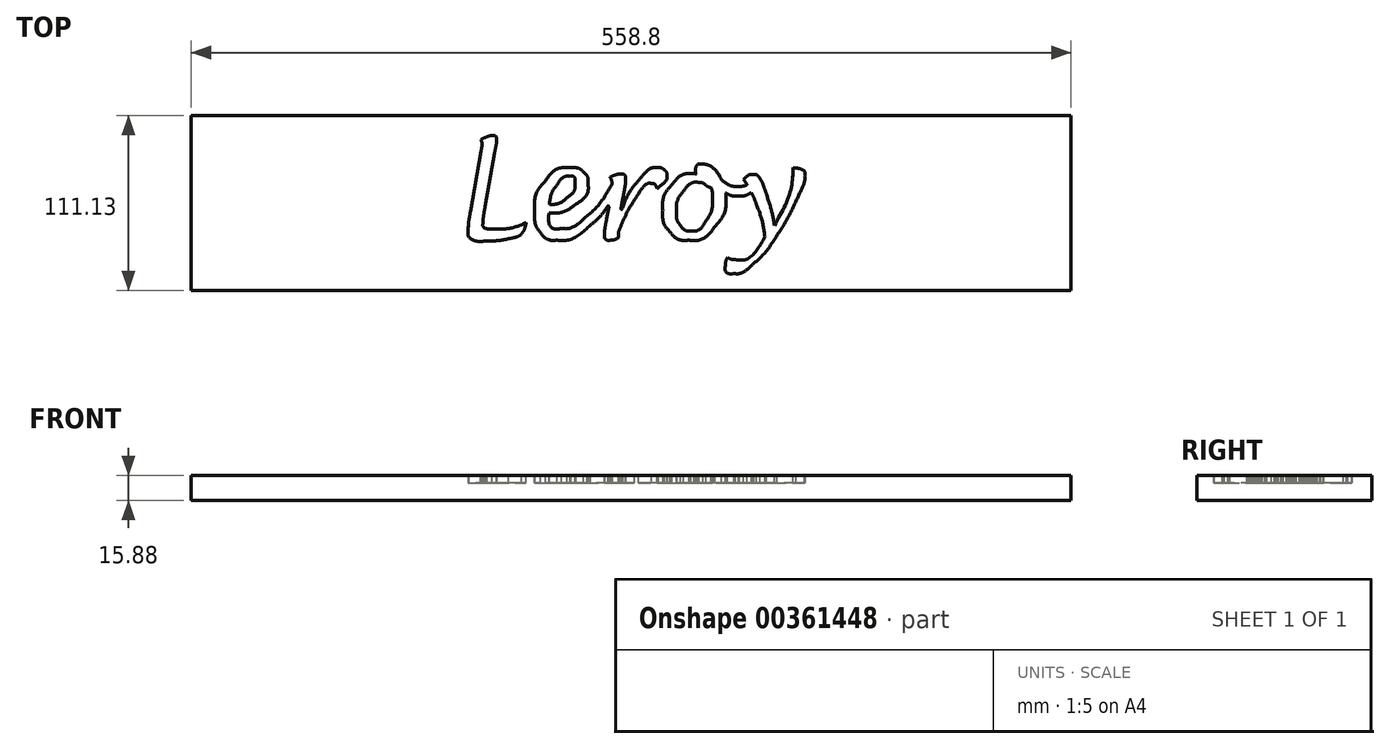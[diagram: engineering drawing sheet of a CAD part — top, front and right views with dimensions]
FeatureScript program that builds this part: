
annotation { "Feature Type Name" : "Feature", "Feature Type Description" : "" }
export const myFeature = defineFeature(function(context is Context, id is Id, definition is map)
    precondition{}
    {
        {
            var Q0;
            Q0=qCreatedBy(makeId("Top.planeOp"),FACE);
            var sketch = newSketch(context, id + "F0", { "sketchPlane" : qUnion([Q0])});
            skLineSegment(sketch, "E0.bottom", {"start": v(12.7, 0) * mm, "end": v(546.1, 0) * mm});
            skLineSegment(sketch, "E0.top", {"start": v(12.7, 609.6) * mm, "end": v(546.1, 609.6) * mm});
            skLineSegment(sketch, "E0.left", {"start": v(0, 12.7) * mm, "end": v(0, 596.9) * mm});
            skLineSegment(sketch, "E0.right", {"start": v(558.8, 12.7) * mm, "end": v(558.8, 596.9) * mm});
            skPoint(sketch, "E1.visualSharp", {"position": v(0, 609.6) * mm});
            skArc(sketch, "E1.filletArc", {"start": v(12.7, 609.6) * mm, "mid": v(3.72, 605.88) * mm, "end": v(0, 596.9) * mm});
            skPoint(sketch, "E2.visualSharp", {"position": v(0, 0) * mm});
            skArc(sketch, "E2.filletArc", {"start": v(0, 12.7) * mm, "mid": v(3.72, 3.72) * mm, "end": v(12.7, 0) * mm});
            skPoint(sketch, "E3.visualSharp", {"position": v(558.8, 0) * mm});
            skArc(sketch, "E3.filletArc", {"start": v(546.1, 0) * mm, "mid": v(555.08, 3.72) * mm, "end": v(558.8, 12.7) * mm});
            skPoint(sketch, "E4.visualSharp", {"position": v(558.8, 609.6) * mm});
            skArc(sketch, "E4.filletArc", {"start": v(558.8, 596.9) * mm, "mid": v(555.08, 605.88) * mm, "end": v(546.1, 609.6) * mm});
            skSolve(sketch);
        }
        {
            var Q0;
            Q0=makeQuery(id+"F0.imprint","IMPRINT",FACE,{"disambiguationData":[TD([[makeQuery(id+"F0.imprint","IMPRINT",EDGE,{"derivedFrom":sQuery(id+"F0.wireOp",EDGE,"E0.bottom")}),1.0]])]});
            extrude(context, id + "F1", {"entities" : qUnion([Q0]), "depth" : 15.88 * mm});
        }
        {
            var Q0;
            Q0=makeQuery(id+"F1.opExtrude","CAP_FACE",FACE,{"disambiguationData":[OSD([sQuery(id+"F0.wireOp",EDGE,"E0.bottom"),sQuery(id+"F0.wireOp",EDGE,"E0.top"),sQuery(id+"F0.wireOp",EDGE,"E0.left"),sQuery(id+"F0.wireOp",EDGE,"E0.right"),sQuery(id+"F0.wireOp",EDGE,"E1.filletArc"),sQuery(id+"F0.wireOp",EDGE,"E2.filletArc"),sQuery(id+"F0.wireOp",EDGE,"E3.filletArc"),sQuery(id+"F0.wireOp",EDGE,"E4.filletArc")])],"isStart":false});
            var sketch = newSketch(context, id + "F2", { "sketchPlane" : qUnion([Q0])});
            skFitSpline(sketch, "E5", {"points": [v(247.46, 485.02) * mm, v(244.22, 485.02) * mm, v(241.38, 482.73) * mm, v(238.94, 478.15) * mm]});
            skFitSpline(sketch, "E6", {"points": [v(238.94, 478.15) * mm, v(236.48, 473.56) * mm, v(235.26, 468.05) * mm, v(235.26, 461.6) * mm]});
            skFitSpline(sketch, "E7", {"points": [v(235.26, 461.6) * mm, v(235.26, 456.87) * mm, v(236.54, 454.5) * mm, v(239.12, 454.5) * mm]});
            skFitSpline(sketch, "E8", {"points": [v(239.12, 454.5) * mm, v(242.2, 454.5) * mm, v(248.34, 462.57) * mm, v(257.6, 478.7) * mm]});
            skFitSpline(sketch, "E9", {"points": [v(257.6, 478.7) * mm, v(257.73, 478.94) * mm, v(258.18, 479.46) * mm, v(258.91, 480.26) * mm]});
            skFitSpline(sketch, "E10", {"points": [v(258.91, 480.26) * mm, v(254.36, 483.44) * mm, v(250.54, 485.02) * mm, v(247.46, 485.02) * mm]});
            skFitSpline(sketch, "E11", {"points": [v(371.38, 485.98) * mm, v(368.47, 485.98) * mm, v(365.74, 484.16) * mm, v(363.18, 480.52) * mm]});
            skFitSpline(sketch, "E12", {"points": [v(363.18, 480.52) * mm, v(360.62, 476.88) * mm, v(359.03, 472.72) * mm, v(358.4, 468.06) * mm]});
            skFitSpline(sketch, "E13", {"points": [v(358.4, 468.06) * mm, v(362.59, 468.32) * mm, v(366.35, 469.82) * mm, v(369.66, 472.53) * mm]});
            skFitSpline(sketch, "E14", {"points": [v(369.66, 472.53) * mm, v(372.98, 475.24) * mm, v(374.64, 478.32) * mm, v(374.64, 481.78) * mm]});
            skFitSpline(sketch, "E15", {"points": [v(374.64, 481.78) * mm, v(374.64, 484.58) * mm, v(373.55, 485.98) * mm, v(371.38, 485.98) * mm]});
            skFitSpline(sketch, "E16", {"points": [v(372.25, 491.45) * mm, v(375.43, 491.45) * mm, v(378, 490.53) * mm, v(379.95, 488.68) * mm]});
            skFitSpline(sketch, "E17", {"points": [v(379.95, 488.68) * mm, v(381.9, 486.84) * mm, v(382.89, 484.38) * mm, v(382.89, 481.3) * mm]});
            skFitSpline(sketch, "E18", {"points": [v(382.89, 481.3) * mm, v(382.89, 476.36) * mm, v(380.3, 472.02) * mm, v(375.12, 468.3) * mm]});
            skFitSpline(sketch, "E19", {"points": [v(375.12, 468.3) * mm, v(369.94, 464.57) * mm, v(364.27, 462.7) * mm, v(358.12, 462.7) * mm]});
            skFitSpline(sketch, "E20", {"points": [v(358.12, 462.7) * mm, v(358.12, 456.15) * mm, v(360.76, 452.87) * mm, v(366.01, 452.87) * mm]});
            skFitSpline(sketch, "E21", {"points": [v(366.01, 452.87) * mm, v(370.84, 452.87) * mm, v(376.2, 455.49) * mm, v(382.13, 460.74) * mm]});
            skFitSpline(sketch, "E22", {"points": [v(382.13, 460.74) * mm, v(388.04, 465.98) * mm, v(393.52, 473.06) * mm, v(398.54, 481.95) * mm]});
            skFitSpline(sketch, "E23", {"points": [v(402.5, 479.62) * mm, v(397.84, 469.55) * mm, v(391.82, 461.33) * mm, v(384.42, 454.98) * mm]});
            skFitSpline(sketch, "E24", {"points": [v(384.42, 454.98) * mm, v(377.03, 448.62) * mm, v(369.98, 445.45) * mm, v(363.3, 445.45) * mm]});
            skFitSpline(sketch, "E25", {"points": [v(363.3, 445.45) * mm, v(358.9, 445.45) * mm, v(355.42, 447.05) * mm, v(352.87, 450.22) * mm]});
            skFitSpline(sketch, "E26", {"points": [v(352.87, 450.22) * mm, v(350.64, 453) * mm, v(349.4, 456.61) * mm, v(349.1, 461.08) * mm]});
            skFitSpline(sketch, "E27", {"points": [v(349.1, 461.08) * mm, v(347.32, 458.56) * mm, v(345.51, 456.33) * mm, v(343.7, 454.35) * mm]});
            skFitSpline(sketch, "E28", {"points": [v(343.7, 454.35) * mm, v(338.24, 448.42) * mm, v(333.27, 445.45) * mm, v(328.8, 445.45) * mm]});
            skFitSpline(sketch, "E29", {"points": [v(328.8, 445.45) * mm, v(325.99, 445.45) * mm, v(323.71, 446.48) * mm, v(322, 448.54) * mm]});
            skFitSpline(sketch, "E30", {"points": [v(322, 448.54) * mm, v(320.27, 450.6) * mm, v(319.41, 453.3) * mm, v(319.41, 456.62) * mm]});
            skFitSpline(sketch, "E31", {"points": [v(319.41, 456.62) * mm, v(319.41, 457.85) * mm, v(319.64, 459.77) * mm, v(320.12, 462.36) * mm]});
            skLineSegment(sketch, "E32", {"start": v(398.54, 481.95) * mm, "end": v(402.5, 479.62) * mm});
            skLineSegment(sketch, "E33", {"start": v(402.5, 479.62) * mm, "end": v(398.54, 481.95) * mm});
            skFitSpline(sketch, "E34", {"points": [v(320.89, 466.68) * mm, v(322, 472.85) * mm, v(322.57, 477.15) * mm, v(322.57, 479.6) * mm]});
            skFitSpline(sketch, "E35", {"points": [v(322.57, 479.6) * mm, v(322.57, 480.87) * mm, v(322.18, 482.24) * mm, v(321.4, 483.7) * mm]});
            skFitSpline(sketch, "E36", {"points": [v(321.4, 483.7) * mm, v(324.84, 484.7) * mm, v(326.97, 485.22) * mm, v(327.78, 485.22) * mm]});
            skFitSpline(sketch, "E37", {"points": [v(327.78, 485.22) * mm, v(329.99, 485.22) * mm, v(331.1, 483.6) * mm, v(331.1, 480.35) * mm]});
            skFitSpline(sketch, "E38", {"points": [v(331.1, 480.35) * mm, v(331.1, 478.32) * mm, v(330.76, 475.38) * mm, v(330.07, 471.54) * mm]});
            skLineSegment(sketch, "E39", {"start": v(320.12, 462.36) * mm, "end": v(320.89, 466.68) * mm});
            skLineSegment(sketch, "E40", {"start": v(320.89, 466.68) * mm, "end": v(320.12, 462.36) * mm});
            skFitSpline(sketch, "E41", {"points": [v(328.7, 463.92) * mm, v(328.05, 460.32) * mm, v(327.73, 458) * mm, v(327.73, 456.92) * mm]});
            skFitSpline(sketch, "E42", {"points": [v(327.73, 456.92) * mm, v(327.73, 454.22) * mm, v(328.7, 452.87) * mm, v(330.64, 452.87) * mm]});
            skFitSpline(sketch, "E43", {"points": [v(330.64, 452.87) * mm, v(333.34, 452.87) * mm, v(337.06, 455.56) * mm, v(341.8, 460.93) * mm]});
            skFitSpline(sketch, "E44", {"points": [v(341.8, 460.93) * mm, v(344.6, 464.12) * mm, v(347.4, 467.87) * mm, v(350.2, 472.2) * mm]});
            skFitSpline(sketch, "E45", {"points": [v(350.2, 472.2) * mm, v(351.28, 476.24) * mm, v(353.16, 479.88) * mm, v(355.83, 483.14) * mm]});
            skFitSpline(sketch, "E46", {"points": [v(355.83, 483.14) * mm, v(360.35, 488.68) * mm, v(365.83, 491.45) * mm, v(372.25, 491.45) * mm]});
            skLineSegment(sketch, "E47", {"start": v(330.07, 471.54) * mm, "end": v(328.7, 463.92) * mm});
            skLineSegment(sketch, "E48", {"start": v(328.7, 463.92) * mm, "end": v(330.07, 471.54) * mm});
            skFitSpline(sketch, "E49", {"points": [v(305.1, 507.84) * mm, v(305.33, 507.84) * mm, v(306.14, 507.78) * mm, v(307.5, 507.65) * mm]});
            skFitSpline(sketch, "E50", {"points": [v(307.5, 507.65) * mm, v(305.64, 504.33) * mm, v(303.76, 499.96) * mm, v(301.86, 494.56) * mm]});
            skFitSpline(sketch, "E51", {"points": [v(319.5, 494.56) * mm, v(322.22, 494.56) * mm, v(324.64, 494.92) * mm, v(326.74, 495.67) * mm]});
            skFitSpline(sketch, "E52", {"points": [v(326.74, 495.67) * mm, v(326.87, 497.05) * mm, v(327.2, 498.41) * mm, v(327.69, 499.77) * mm]});
            skLineSegment(sketch, "E53", {"start": v(301.86, 494.56) * mm, "end": v(319.5, 494.56) * mm});
            skLineSegment(sketch, "E54", {"start": v(319.5, 494.56) * mm, "end": v(301.86, 494.56) * mm});
            skFitSpline(sketch, "E55", {"points": [v(328.67, 499.72) * mm, v(330.08, 499.79) * mm, v(332.2, 500.64) * mm, v(335.04, 502.28) * mm]});
            skFitSpline(sketch, "E56", {"points": [v(335.04, 502.28) * mm, v(337.9, 503.93) * mm, v(340.52, 505.68) * mm, v(342.94, 507.52) * mm]});
            skFitSpline(sketch, "E57", {"points": [v(342.94, 507.52) * mm, v(341.85, 503.08) * mm, v(340.03, 500.06) * mm, v(337.5, 498.48) * mm]});
            skFitSpline(sketch, "E58", {"points": [v(337.5, 498.48) * mm, v(333.26, 493.7) * mm, v(330.34, 491.32) * mm, v(328.76, 491.32) * mm]});
            skFitSpline(sketch, "E59", {"points": [v(328.76, 491.32) * mm, v(327.76, 491.32) * mm, v(327.1, 491.79) * mm, v(326.85, 492.72) * mm]});
            skFitSpline(sketch, "E60", {"points": [v(326.85, 492.72) * mm, v(326.33, 491.05) * mm, v(325.73, 489.92) * mm, v(325.02, 489.33) * mm]});
            skFitSpline(sketch, "E61", {"points": [v(325.02, 489.33) * mm, v(323.92, 488.4) * mm, v(321.98, 487.93) * mm, v(319.18, 487.93) * mm]});
            skLineSegment(sketch, "E62", {"start": v(327.69, 499.77) * mm, "end": v(328.67, 499.72) * mm});
            skLineSegment(sketch, "E63", {"start": v(328.67, 499.72) * mm, "end": v(327.69, 499.77) * mm});
            skFitSpline(sketch, "E64", {"points": [v(300.17, 487.93) * mm, v(300.04, 487.44) * mm, v(299.9, 486.92) * mm, v(299.75, 486.38) * mm]});
            skFitSpline(sketch, "E65", {"points": [v(299.75, 486.38) * mm, v(296.99, 475.84) * mm, v(295.6, 467.88) * mm, v(295.6, 462.47) * mm]});
            skFitSpline(sketch, "E66", {"points": [v(295.6, 462.47) * mm, v(295.6, 456.94) * mm, v(297.3, 454.18) * mm, v(300.68, 454.18) * mm]});
            skFitSpline(sketch, "E67", {"points": [v(300.68, 454.18) * mm, v(302.53, 454.18) * mm, v(304.57, 455.1) * mm, v(306.8, 456.9) * mm]});
            skFitSpline(sketch, "E68", {"points": [v(306.8, 456.9) * mm, v(309.05, 458.71) * mm, v(310.85, 460.91) * mm, v(312.2, 463.5) * mm]});
            skFitSpline(sketch, "E69", {"points": [v(312.2, 463.5) * mm, v(313.35, 461.8) * mm, v(313.92, 460.42) * mm, v(313.92, 459.33) * mm]});
            skFitSpline(sketch, "E70", {"points": [v(313.92, 459.33) * mm, v(313.92, 456.5) * mm, v(311.92, 453.5) * mm, v(307.92, 450.28) * mm]});
            skFitSpline(sketch, "E71", {"points": [v(307.92, 450.28) * mm, v(303.9, 447.06) * mm, v(300.24, 445.45) * mm, v(296.9, 445.45) * mm]});
            skFitSpline(sketch, "E72", {"points": [v(296.9, 445.45) * mm, v(293.88, 445.45) * mm, v(291.42, 446.93) * mm, v(289.56, 449.9) * mm]});
            skFitSpline(sketch, "E73", {"points": [v(289.56, 449.9) * mm, v(287.7, 452.87) * mm, v(286.76, 456.65) * mm, v(286.76, 461.23) * mm]});
            skFitSpline(sketch, "E74", {"points": [v(286.76, 461.23) * mm, v(286.76, 462.58) * mm, v(286.84, 464.08) * mm, v(287.02, 465.75) * mm]});
            skFitSpline(sketch, "E75", {"points": [v(287.02, 465.75) * mm, v(284.81, 462.56) * mm, v(282.47, 459.69) * mm, v(280.01, 457.13) * mm]});
            skFitSpline(sketch, "E76", {"points": [v(280.01, 457.13) * mm, v(274.37, 451.28) * mm, v(269.48, 448.36) * mm, v(265.31, 448.36) * mm]});
            skFitSpline(sketch, "E77", {"points": [v(265.31, 448.36) * mm, v(259.81, 448.36) * mm, v(257.07, 453.3) * mm, v(257.07, 463.23) * mm]});
            skFitSpline(sketch, "E78", {"points": [v(257.07, 463.23) * mm, v(257.07, 465.2) * mm, v(257.14, 467.57) * mm, v(257.28, 470.32) * mm]});
            skFitSpline(sketch, "E79", {"points": [v(257.28, 470.32) * mm, v(255.19, 463.64) * mm, v(251.91, 457.83) * mm, v(247.46, 452.87) * mm]});
            skFitSpline(sketch, "E80", {"points": [v(247.46, 452.87) * mm, v(242.99, 447.92) * mm, v(239.04, 445.45) * mm, v(235.6, 445.45) * mm]});
            skFitSpline(sketch, "E81", {"points": [v(235.6, 445.45) * mm, v(232.88, 445.45) * mm, v(230.72, 446.77) * mm, v(229.15, 449.4) * mm]});
            skFitSpline(sketch, "E82", {"points": [v(229.15, 449.4) * mm, v(227.56, 452.05) * mm, v(226.77, 455.51) * mm, v(226.77, 459.78) * mm]});
            skFitSpline(sketch, "E83", {"points": [v(226.77, 459.78) * mm, v(226.77, 468.13) * mm, v(229.03, 475.5) * mm, v(233.56, 481.87) * mm]});
            skFitSpline(sketch, "E84", {"points": [v(233.56, 481.87) * mm, v(238.09, 488.26) * mm, v(243.35, 491.45) * mm, v(249.38, 491.45) * mm]});
            skFitSpline(sketch, "E85", {"points": [v(249.38, 491.45) * mm, v(253.01, 491.45) * mm, v(256.66, 490.21) * mm, v(260.33, 487.76) * mm]});
            skFitSpline(sketch, "E86", {"points": [v(260.33, 487.76) * mm, v(260.86, 490.19) * mm, v(263.48, 491.4) * mm, v(268.16, 491.4) * mm]});
            skFitSpline(sketch, "E87", {"points": [v(268.16, 491.4) * mm, v(268.26, 491.4) * mm, v(268.96, 491.37) * mm, v(270.27, 491.3) * mm]});
            skFitSpline(sketch, "E88", {"points": [v(270.27, 491.3) * mm, v(268.9, 488.33) * mm, v(267.89, 484.93) * mm, v(267.2, 481.1) * mm]});
            skLineSegment(sketch, "E89", {"start": v(319.18, 487.93) * mm, "end": v(300.17, 487.93) * mm});
            skLineSegment(sketch, "E90", {"start": v(300.17, 487.93) * mm, "end": v(319.18, 487.93) * mm});
            skFitSpline(sketch, "E91", {"points": [v(266.62, 477.77) * mm, v(265.96, 474.15) * mm, v(265.63, 469.88) * mm, v(265.63, 464.94) * mm]});
            skFitSpline(sketch, "E92", {"points": [v(265.63, 464.94) * mm, v(265.63, 459.77) * mm, v(266.57, 457.18) * mm, v(268.44, 457.18) * mm]});
            skFitSpline(sketch, "E93", {"points": [v(268.44, 457.18) * mm, v(270.76, 457.18) * mm, v(274.05, 459.48) * mm, v(278.32, 464.1) * mm]});
            skFitSpline(sketch, "E94", {"points": [v(278.32, 464.1) * mm, v(281.96, 468.04) * mm, v(285.66, 473) * mm, v(289.42, 478.98) * mm]});
            skFitSpline(sketch, "E95", {"points": [v(289.42, 478.98) * mm, v(289.7, 480.18) * mm, v(290, 481.4) * mm, v(290.32, 482.69) * mm]});
            skLineSegment(sketch, "E96", {"start": v(267.2, 481.1) * mm, "end": v(266.62, 477.77) * mm});
            skLineSegment(sketch, "E97", {"start": v(266.62, 477.77) * mm, "end": v(267.2, 481.1) * mm});
            skFitSpline(sketch, "E98", {"points": [v(286.65, 487.93) * mm, v(284.3, 487.93) * mm, v(282.1, 487.54) * mm, v(280.04, 486.76) * mm]});
            skFitSpline(sketch, "E99", {"points": [v(280.04, 486.76) * mm, v(281.5, 490.38) * mm, v(282.72, 492.6) * mm, v(283.72, 493.38) * mm]});
            skFitSpline(sketch, "E100", {"points": [v(283.72, 493.38) * mm, v(284.71, 494.16) * mm, v(286.34, 494.56) * mm, v(288.6, 494.56) * mm]});
            skLineSegment(sketch, "E101", {"start": v(290.32, 482.69) * mm, "end": v(291.82, 487.93) * mm});
            skLineSegment(sketch, "E102", {"start": v(291.82, 487.93) * mm, "end": v(286.65, 487.93) * mm});
            skFitSpline(sketch, "E103", {"points": [v(293.99, 497.12) * mm, v(295.02, 501) * mm, v(296.33, 503.76) * mm, v(297.95, 505.4) * mm]});
            skFitSpline(sketch, "E104", {"points": [v(297.95, 505.4) * mm, v(299.55, 507.03) * mm, v(301.94, 507.84) * mm, v(305.1, 507.84) * mm]});
            skLineSegment(sketch, "E105", {"start": v(288.6, 494.56) * mm, "end": v(293.33, 494.56) * mm});
            skLineSegment(sketch, "E106", {"start": v(293.33, 494.56) * mm, "end": v(293.99, 497.12) * mm});
            skFitSpline(sketch, "E107", {"points": [v(178.41, 506.2) * mm, v(181.96, 506.2) * mm, v(186.85, 506.6) * mm, v(193.08, 507.4) * mm]});
            skFitSpline(sketch, "E108", {"points": [v(188.04, 478.85) * mm, v(200.42, 488.81) * mm, v(207.85, 498.44) * mm, v(210.33, 507.7) * mm]});
            skFitSpline(sketch, "E109", {"points": [v(210.33, 507.7) * mm, v(214.42, 505.56) * mm, v(216.46, 503.26) * mm, v(216.46, 500.79) * mm]});
            skFitSpline(sketch, "E110", {"points": [v(216.46, 500.79) * mm, v(216.46, 499.37) * mm, v(213.98, 496.13) * mm, v(209, 491.1) * mm]});
            skFitSpline(sketch, "E111", {"points": [v(209, 491.1) * mm, v(204.02, 486.08) * mm, v(199.1, 481.73) * mm, v(194.23, 478.07) * mm]});
            skFitSpline(sketch, "E112", {"points": [v(194.23, 478.07) * mm, v(198.39, 469.54) * mm, v(202.46, 462.52) * mm, v(206.43, 457.03) * mm]});
            skFitSpline(sketch, "E113", {"points": [v(206.43, 457.03) * mm, v(210.4, 451.54) * mm, v(213.38, 448.8) * mm, v(215.37, 448.8) * mm]});
            skFitSpline(sketch, "E114", {"points": [v(215.37, 448.8) * mm, v(217.55, 448.8) * mm, v(220.39, 450.27) * mm, v(223.87, 453.22) * mm]});
            skLineSegment(sketch, "E115", {"start": v(193.08, 507.4) * mm, "end": v(188.04, 478.85) * mm});
            skLineSegment(sketch, "E116", {"start": v(188.04, 478.85) * mm, "end": v(193.08, 507.4) * mm});
            skFitSpline(sketch, "E117", {"points": [v(223.98, 451.1) * mm, v(223.98, 449.09) * mm, v(222.68, 446.98) * mm, v(220.08, 444.73) * mm]});
            skFitSpline(sketch, "E118", {"points": [v(220.08, 444.73) * mm, v(217.49, 442.5) * mm, v(214.96, 441.38) * mm, v(212.51, 441.38) * mm]});
            skFitSpline(sketch, "E119", {"points": [v(212.51, 441.38) * mm, v(206.3, 441.38) * mm, v(197.85, 452.5) * mm, v(187.18, 474.76) * mm]});
            skLineSegment(sketch, "E120", {"start": v(223.87, 453.22) * mm, "end": v(223.98, 451.1) * mm});
            skLineSegment(sketch, "E121", {"start": v(223.98, 451.1) * mm, "end": v(223.87, 453.22) * mm});
            skFitSpline(sketch, "E122", {"points": [v(183.9, 454.8) * mm, v(183.48, 452.44) * mm, v(183.27, 450.88) * mm, v(183.27, 450.14) * mm]});
            skFitSpline(sketch, "E123", {"points": [v(183.27, 450.14) * mm, v(183.27, 449.5) * mm, v(183.42, 448.6) * mm, v(183.73, 447.42) * mm]});
            skFitSpline(sketch, "E124", {"points": [v(183.73, 447.42) * mm, v(180.96, 445.82) * mm, v(178.55, 445.01) * mm, v(176.52, 445.01) * mm]});
            skFitSpline(sketch, "E125", {"points": [v(176.52, 445.01) * mm, v(174.84, 445.01) * mm, v(174, 445.83) * mm, v(174, 447.45) * mm]});
            skFitSpline(sketch, "E126", {"points": [v(174, 447.45) * mm, v(174, 448.08) * mm, v(174.25, 449.8) * mm, v(174.74, 452.56) * mm]});
            skLineSegment(sketch, "E127", {"start": v(187.18, 474.76) * mm, "end": v(183.9, 454.8) * mm});
            skLineSegment(sketch, "E128", {"start": v(183.9, 454.8) * mm, "end": v(187.18, 474.76) * mm});
            skFitSpline(sketch, "E129", {"points": [v(183.17, 499.25) * mm, v(181.66, 498.94) * mm, v(180, 498.79) * mm, v(178.17, 498.79) * mm]});
            skFitSpline(sketch, "E130", {"points": [v(178.17, 498.79) * mm, v(174.1, 498.79) * mm, v(171.7, 502.02) * mm, v(170.94, 508.51) * mm]});
            skLineSegment(sketch, "E131", {"start": v(174.74, 452.56) * mm, "end": v(183.17, 499.25) * mm});
            skLineSegment(sketch, "E132", {"start": v(183.17, 499.25) * mm, "end": v(174.74, 452.56) * mm});
            skFitSpline(sketch, "E133", {"points": [v(247.46, 485.02) * mm, v(244.22, 485.02) * mm, v(241.38, 482.73) * mm, v(238.94, 478.15) * mm]});
            skFitSpline(sketch, "E134", {"points": [v(238.94, 478.15) * mm, v(236.48, 473.56) * mm, v(235.26, 468.05) * mm, v(235.26, 461.6) * mm]});
            skFitSpline(sketch, "E135", {"points": [v(235.26, 461.6) * mm, v(235.26, 456.87) * mm, v(236.54, 454.5) * mm, v(239.12, 454.5) * mm]});
            skFitSpline(sketch, "E136", {"points": [v(239.12, 454.5) * mm, v(242.2, 454.5) * mm, v(248.34, 462.57) * mm, v(257.6, 478.7) * mm]});
            skFitSpline(sketch, "E137", {"points": [v(257.6, 478.7) * mm, v(257.73, 478.94) * mm, v(258.18, 479.46) * mm, v(258.91, 480.26) * mm]});
            skFitSpline(sketch, "E138", {"points": [v(258.91, 480.26) * mm, v(254.36, 483.44) * mm, v(250.54, 485.02) * mm, v(247.46, 485.02) * mm]});
            skFitSpline(sketch, "E139", {"points": [v(371.38, 485.98) * mm, v(368.47, 485.98) * mm, v(365.74, 484.16) * mm, v(363.18, 480.52) * mm]});
            skFitSpline(sketch, "E140", {"points": [v(363.18, 480.52) * mm, v(360.62, 476.88) * mm, v(359.03, 472.72) * mm, v(358.4, 468.06) * mm]});
            skFitSpline(sketch, "E141", {"points": [v(358.4, 468.06) * mm, v(362.59, 468.32) * mm, v(366.35, 469.82) * mm, v(369.66, 472.53) * mm]});
            skFitSpline(sketch, "E142", {"points": [v(369.66, 472.53) * mm, v(372.98, 475.24) * mm, v(374.64, 478.32) * mm, v(374.64, 481.78) * mm]});
            skFitSpline(sketch, "E143", {"points": [v(374.64, 481.78) * mm, v(374.64, 484.58) * mm, v(373.55, 485.98) * mm, v(371.38, 485.98) * mm]});
            skFitSpline(sketch, "E144", {"points": [v(372.25, 491.45) * mm, v(375.43, 491.45) * mm, v(378, 490.53) * mm, v(379.95, 488.68) * mm]});
            skFitSpline(sketch, "E145", {"points": [v(379.95, 488.68) * mm, v(381.9, 486.84) * mm, v(382.89, 484.38) * mm, v(382.89, 481.3) * mm]});
            skFitSpline(sketch, "E146", {"points": [v(382.89, 481.3) * mm, v(382.89, 476.36) * mm, v(380.3, 472.02) * mm, v(375.12, 468.3) * mm]});
            skFitSpline(sketch, "E147", {"points": [v(375.12, 468.3) * mm, v(369.94, 464.57) * mm, v(364.27, 462.7) * mm, v(358.12, 462.7) * mm]});
            skFitSpline(sketch, "E148", {"points": [v(358.12, 462.7) * mm, v(358.12, 456.15) * mm, v(360.76, 452.87) * mm, v(366.01, 452.87) * mm]});
            skFitSpline(sketch, "E149", {"points": [v(366.01, 452.87) * mm, v(370.84, 452.87) * mm, v(376.2, 455.49) * mm, v(382.13, 460.74) * mm]});
            skFitSpline(sketch, "E150", {"points": [v(382.13, 460.74) * mm, v(388.04, 465.98) * mm, v(393.52, 473.06) * mm, v(398.54, 481.95) * mm]});
            skFitSpline(sketch, "E151", {"points": [v(402.5, 479.62) * mm, v(397.84, 469.55) * mm, v(391.82, 461.33) * mm, v(384.42, 454.98) * mm]});
            skFitSpline(sketch, "E152", {"points": [v(384.42, 454.98) * mm, v(377.03, 448.62) * mm, v(369.98, 445.45) * mm, v(363.3, 445.45) * mm]});
            skFitSpline(sketch, "E153", {"points": [v(363.3, 445.45) * mm, v(358.9, 445.45) * mm, v(355.42, 447.05) * mm, v(352.87, 450.22) * mm]});
            skFitSpline(sketch, "E154", {"points": [v(352.87, 450.22) * mm, v(350.64, 453) * mm, v(349.4, 456.61) * mm, v(349.1, 461.08) * mm]});
            skFitSpline(sketch, "E155", {"points": [v(349.1, 461.08) * mm, v(347.32, 458.56) * mm, v(345.51, 456.33) * mm, v(343.7, 454.35) * mm]});
            skFitSpline(sketch, "E156", {"points": [v(343.7, 454.35) * mm, v(338.24, 448.42) * mm, v(333.27, 445.45) * mm, v(328.8, 445.45) * mm]});
            skFitSpline(sketch, "E157", {"points": [v(328.8, 445.45) * mm, v(325.99, 445.45) * mm, v(323.71, 446.48) * mm, v(322, 448.54) * mm]});
            skFitSpline(sketch, "E158", {"points": [v(322, 448.54) * mm, v(320.27, 450.6) * mm, v(319.41, 453.3) * mm, v(319.41, 456.62) * mm]});
            skFitSpline(sketch, "E159", {"points": [v(319.41, 456.62) * mm, v(319.41, 457.85) * mm, v(319.64, 459.77) * mm, v(320.12, 462.36) * mm]});
            skFitSpline(sketch, "E160", {"points": [v(320.89, 466.68) * mm, v(322, 472.85) * mm, v(322.57, 477.15) * mm, v(322.57, 479.6) * mm]});
            skFitSpline(sketch, "E161", {"points": [v(322.57, 479.6) * mm, v(322.57, 480.87) * mm, v(322.18, 482.24) * mm, v(321.4, 483.7) * mm]});
            skFitSpline(sketch, "E162", {"points": [v(321.4, 483.7) * mm, v(324.84, 484.7) * mm, v(326.97, 485.22) * mm, v(327.78, 485.22) * mm]});
            skFitSpline(sketch, "E163", {"points": [v(327.78, 485.22) * mm, v(329.99, 485.22) * mm, v(331.1, 483.6) * mm, v(331.1, 480.35) * mm]});
            skFitSpline(sketch, "E164", {"points": [v(331.1, 480.35) * mm, v(331.1, 478.32) * mm, v(330.76, 475.38) * mm, v(330.07, 471.54) * mm]});
            skFitSpline(sketch, "E165", {"points": [v(328.7, 463.92) * mm, v(328.05, 460.32) * mm, v(327.73, 458) * mm, v(327.73, 456.92) * mm]});
            skFitSpline(sketch, "E166", {"points": [v(327.73, 456.92) * mm, v(327.73, 454.22) * mm, v(328.7, 452.87) * mm, v(330.64, 452.87) * mm]});
            skFitSpline(sketch, "E167", {"points": [v(330.64, 452.87) * mm, v(333.34, 452.87) * mm, v(337.06, 455.56) * mm, v(341.8, 460.93) * mm]});
            skFitSpline(sketch, "E168", {"points": [v(341.8, 460.93) * mm, v(344.6, 464.12) * mm, v(347.4, 467.87) * mm, v(350.2, 472.2) * mm]});
            skFitSpline(sketch, "E169", {"points": [v(350.2, 472.2) * mm, v(351.28, 476.24) * mm, v(353.16, 479.88) * mm, v(355.83, 483.14) * mm]});
            skFitSpline(sketch, "E170", {"points": [v(355.83, 483.14) * mm, v(360.35, 488.68) * mm, v(365.83, 491.45) * mm, v(372.25, 491.45) * mm]});
            skFitSpline(sketch, "E171", {"points": [v(305.1, 507.84) * mm, v(305.33, 507.84) * mm, v(306.14, 507.78) * mm, v(307.5, 507.65) * mm]});
            skFitSpline(sketch, "E172", {"points": [v(307.5, 507.65) * mm, v(305.64, 504.33) * mm, v(303.76, 499.96) * mm, v(301.86, 494.56) * mm]});
            skFitSpline(sketch, "E173", {"points": [v(319.5, 494.56) * mm, v(322.22, 494.56) * mm, v(324.64, 494.92) * mm, v(326.74, 495.67) * mm]});
            skFitSpline(sketch, "E174", {"points": [v(326.74, 495.67) * mm, v(326.87, 497.05) * mm, v(327.2, 498.41) * mm, v(327.69, 499.77) * mm]});
            skFitSpline(sketch, "E175", {"points": [v(328.67, 499.72) * mm, v(330.08, 499.79) * mm, v(332.2, 500.64) * mm, v(335.04, 502.28) * mm]});
            skFitSpline(sketch, "E176", {"points": [v(335.04, 502.28) * mm, v(337.9, 503.93) * mm, v(340.52, 505.68) * mm, v(342.94, 507.52) * mm]});
            skFitSpline(sketch, "E177", {"points": [v(342.94, 507.52) * mm, v(341.85, 503.08) * mm, v(340.03, 500.06) * mm, v(337.5, 498.48) * mm]});
            skFitSpline(sketch, "E178", {"points": [v(337.5, 498.48) * mm, v(333.26, 493.7) * mm, v(330.34, 491.32) * mm, v(328.76, 491.32) * mm]});
            skFitSpline(sketch, "E179", {"points": [v(328.76, 491.32) * mm, v(327.76, 491.32) * mm, v(327.1, 491.79) * mm, v(326.85, 492.72) * mm]});
            skFitSpline(sketch, "E180", {"points": [v(326.85, 492.72) * mm, v(326.33, 491.05) * mm, v(325.73, 489.92) * mm, v(325.02, 489.33) * mm]});
            skFitSpline(sketch, "E181", {"points": [v(325.02, 489.33) * mm, v(323.92, 488.4) * mm, v(321.98, 487.93) * mm, v(319.18, 487.93) * mm]});
            skFitSpline(sketch, "E182", {"points": [v(300.17, 487.93) * mm, v(300.04, 487.44) * mm, v(299.9, 486.92) * mm, v(299.75, 486.38) * mm]});
            skFitSpline(sketch, "E183", {"points": [v(299.75, 486.38) * mm, v(296.99, 475.84) * mm, v(295.6, 467.88) * mm, v(295.6, 462.47) * mm]});
            skFitSpline(sketch, "E184", {"points": [v(295.6, 462.47) * mm, v(295.6, 456.94) * mm, v(297.3, 454.18) * mm, v(300.68, 454.18) * mm]});
            skFitSpline(sketch, "E185", {"points": [v(300.68, 454.18) * mm, v(302.53, 454.18) * mm, v(304.57, 455.1) * mm, v(306.8, 456.9) * mm]});
            skFitSpline(sketch, "E186", {"points": [v(306.8, 456.9) * mm, v(309.05, 458.71) * mm, v(310.85, 460.91) * mm, v(312.2, 463.5) * mm]});
            skFitSpline(sketch, "E187", {"points": [v(312.2, 463.5) * mm, v(313.35, 461.8) * mm, v(313.92, 460.42) * mm, v(313.92, 459.33) * mm]});
            skFitSpline(sketch, "E188", {"points": [v(313.92, 459.33) * mm, v(313.92, 456.5) * mm, v(311.92, 453.5) * mm, v(307.92, 450.28) * mm]});
            skFitSpline(sketch, "E189", {"points": [v(307.92, 450.28) * mm, v(303.9, 447.06) * mm, v(300.24, 445.45) * mm, v(296.9, 445.45) * mm]});
            skFitSpline(sketch, "E190", {"points": [v(296.9, 445.45) * mm, v(293.88, 445.45) * mm, v(291.42, 446.93) * mm, v(289.56, 449.9) * mm]});
            skFitSpline(sketch, "E191", {"points": [v(289.56, 449.9) * mm, v(287.7, 452.87) * mm, v(286.76, 456.65) * mm, v(286.76, 461.23) * mm]});
            skFitSpline(sketch, "E192", {"points": [v(286.76, 461.23) * mm, v(286.76, 462.58) * mm, v(286.84, 464.08) * mm, v(287.02, 465.75) * mm]});
            skFitSpline(sketch, "E193", {"points": [v(287.02, 465.75) * mm, v(284.81, 462.56) * mm, v(282.47, 459.69) * mm, v(280.01, 457.13) * mm]});
            skFitSpline(sketch, "E194", {"points": [v(280.01, 457.13) * mm, v(274.37, 451.28) * mm, v(269.48, 448.36) * mm, v(265.31, 448.36) * mm]});
            skFitSpline(sketch, "E195", {"points": [v(265.31, 448.36) * mm, v(259.81, 448.36) * mm, v(257.07, 453.3) * mm, v(257.07, 463.23) * mm]});
            skFitSpline(sketch, "E196", {"points": [v(257.07, 463.23) * mm, v(257.07, 465.2) * mm, v(257.14, 467.57) * mm, v(257.28, 470.32) * mm]});
            skFitSpline(sketch, "E197", {"points": [v(257.28, 470.32) * mm, v(255.19, 463.64) * mm, v(251.91, 457.83) * mm, v(247.46, 452.87) * mm]});
            skFitSpline(sketch, "E198", {"points": [v(247.46, 452.87) * mm, v(242.99, 447.92) * mm, v(239.04, 445.45) * mm, v(235.6, 445.45) * mm]});
            skFitSpline(sketch, "E199", {"points": [v(235.6, 445.45) * mm, v(232.88, 445.45) * mm, v(230.72, 446.77) * mm, v(229.15, 449.4) * mm]});
            skFitSpline(sketch, "E200", {"points": [v(229.15, 449.4) * mm, v(227.56, 452.05) * mm, v(226.77, 455.51) * mm, v(226.77, 459.78) * mm]});
            skFitSpline(sketch, "E201", {"points": [v(226.77, 459.78) * mm, v(226.77, 468.13) * mm, v(229.03, 475.5) * mm, v(233.56, 481.87) * mm]});
            skFitSpline(sketch, "E202", {"points": [v(233.56, 481.87) * mm, v(238.09, 488.26) * mm, v(243.35, 491.45) * mm, v(249.38, 491.45) * mm]});
            skFitSpline(sketch, "E203", {"points": [v(249.38, 491.45) * mm, v(253.01, 491.45) * mm, v(256.66, 490.21) * mm, v(260.33, 487.76) * mm]});
            skFitSpline(sketch, "E204", {"points": [v(260.33, 487.76) * mm, v(260.86, 490.19) * mm, v(263.48, 491.4) * mm, v(268.16, 491.4) * mm]});
            skFitSpline(sketch, "E205", {"points": [v(268.16, 491.4) * mm, v(268.26, 491.4) * mm, v(268.96, 491.37) * mm, v(270.27, 491.3) * mm]});
            skFitSpline(sketch, "E206", {"points": [v(270.27, 491.3) * mm, v(268.9, 488.33) * mm, v(267.89, 484.93) * mm, v(267.2, 481.1) * mm]});
            skFitSpline(sketch, "E207", {"points": [v(266.62, 477.77) * mm, v(265.96, 474.15) * mm, v(265.63, 469.88) * mm, v(265.63, 464.94) * mm]});
            skFitSpline(sketch, "E208", {"points": [v(265.63, 464.94) * mm, v(265.63, 459.77) * mm, v(266.57, 457.18) * mm, v(268.44, 457.18) * mm]});
            skFitSpline(sketch, "E209", {"points": [v(268.44, 457.18) * mm, v(270.76, 457.18) * mm, v(274.05, 459.48) * mm, v(278.32, 464.1) * mm]});
            skFitSpline(sketch, "E210", {"points": [v(278.32, 464.1) * mm, v(281.96, 468.04) * mm, v(285.66, 473) * mm, v(289.42, 478.98) * mm]});
            skFitSpline(sketch, "E211", {"points": [v(289.42, 478.98) * mm, v(289.7, 480.18) * mm, v(290, 481.4) * mm, v(290.32, 482.69) * mm]});
            skFitSpline(sketch, "E212", {"points": [v(286.65, 487.93) * mm, v(284.3, 487.93) * mm, v(282.1, 487.54) * mm, v(280.04, 486.76) * mm]});
            skFitSpline(sketch, "E213", {"points": [v(280.04, 486.76) * mm, v(281.5, 490.38) * mm, v(282.72, 492.6) * mm, v(283.72, 493.38) * mm]});
            skFitSpline(sketch, "E214", {"points": [v(283.72, 493.38) * mm, v(284.71, 494.16) * mm, v(286.34, 494.56) * mm, v(288.6, 494.56) * mm]});
            skFitSpline(sketch, "E215", {"points": [v(293.99, 497.12) * mm, v(295.02, 501) * mm, v(296.33, 503.76) * mm, v(297.95, 505.4) * mm]});
            skFitSpline(sketch, "E216", {"points": [v(297.95, 505.4) * mm, v(299.55, 507.03) * mm, v(301.94, 507.84) * mm, v(305.1, 507.84) * mm]});
            skFitSpline(sketch, "E217", {"points": [v(170.94, 508.51) * mm, v(173.27, 506.97) * mm, v(175.75, 506.2) * mm, v(178.41, 506.2) * mm]});
            skFitSpline(sketch, "E218", {"points": [v(178.41, 506.2) * mm, v(181.96, 506.2) * mm, v(186.85, 506.6) * mm, v(193.08, 507.4) * mm]});
            skFitSpline(sketch, "E219", {"points": [v(188.04, 478.85) * mm, v(200.42, 488.81) * mm, v(207.85, 498.44) * mm, v(210.33, 507.7) * mm]});
            skFitSpline(sketch, "E220", {"points": [v(210.33, 507.7) * mm, v(214.42, 505.56) * mm, v(216.46, 503.26) * mm, v(216.46, 500.79) * mm]});
            skFitSpline(sketch, "E221", {"points": [v(216.46, 500.79) * mm, v(216.46, 499.37) * mm, v(213.98, 496.13) * mm, v(209, 491.1) * mm]});
            skFitSpline(sketch, "E222", {"points": [v(209, 491.1) * mm, v(204.02, 486.08) * mm, v(199.1, 481.73) * mm, v(194.23, 478.07) * mm]});
            skFitSpline(sketch, "E223", {"points": [v(194.23, 478.07) * mm, v(198.39, 469.54) * mm, v(202.46, 462.52) * mm, v(206.43, 457.03) * mm]});
            skFitSpline(sketch, "E224", {"points": [v(206.43, 457.03) * mm, v(210.4, 451.54) * mm, v(213.38, 448.8) * mm, v(215.37, 448.8) * mm]});
            skFitSpline(sketch, "E225", {"points": [v(215.37, 448.8) * mm, v(217.55, 448.8) * mm, v(220.39, 450.27) * mm, v(223.87, 453.22) * mm]});
            skFitSpline(sketch, "E226", {"points": [v(223.98, 451.1) * mm, v(223.98, 449.09) * mm, v(222.68, 446.98) * mm, v(220.08, 444.73) * mm]});
            skFitSpline(sketch, "E227", {"points": [v(220.08, 444.73) * mm, v(217.49, 442.5) * mm, v(214.96, 441.38) * mm, v(212.51, 441.38) * mm]});
            skFitSpline(sketch, "E228", {"points": [v(212.51, 441.38) * mm, v(206.3, 441.38) * mm, v(197.85, 452.5) * mm, v(187.18, 474.76) * mm]});
            skFitSpline(sketch, "E229", {"points": [v(183.9, 454.8) * mm, v(183.48, 452.44) * mm, v(183.27, 450.88) * mm, v(183.27, 450.14) * mm]});
            skFitSpline(sketch, "E230", {"points": [v(183.27, 450.14) * mm, v(183.27, 449.5) * mm, v(183.42, 448.6) * mm, v(183.73, 447.42) * mm]});
            skFitSpline(sketch, "E231", {"points": [v(183.73, 447.42) * mm, v(180.96, 445.82) * mm, v(178.55, 445.01) * mm, v(176.52, 445.01) * mm]});
            skFitSpline(sketch, "E232", {"points": [v(176.52, 445.01) * mm, v(174.84, 445.01) * mm, v(174, 445.83) * mm, v(174, 447.45) * mm]});
            skFitSpline(sketch, "E233", {"points": [v(174, 447.45) * mm, v(174, 448.08) * mm, v(174.25, 449.8) * mm, v(174.74, 452.56) * mm]});
            skFitSpline(sketch, "E234", {"points": [v(183.17, 499.25) * mm, v(181.66, 498.94) * mm, v(180, 498.79) * mm, v(178.17, 498.79) * mm]});
            skFitSpline(sketch, "E235", {"points": [v(178.17, 498.79) * mm, v(174.1, 498.79) * mm, v(171.7, 502.02) * mm, v(170.94, 508.51) * mm]});
            skFitSpline(sketch, "E236", {"points": [v(277.79, 394.65) * mm, v(280.95, 394.65) * mm, v(283.67, 394.04) * mm, v(285.93, 392.83) * mm]});
            skFitSpline(sketch, "E237", {"points": [v(285.93, 392.83) * mm, v(288.2, 391.61) * mm, v(289.33, 390.05) * mm, v(289.33, 388.1) * mm]});
            skFitSpline(sketch, "E238", {"points": [v(289.33, 388.1) * mm, v(289.33, 386.55) * mm, v(288.3, 384.9) * mm, v(286.28, 383.13) * mm]});
            skFitSpline(sketch, "E239", {"points": [v(286.28, 383.13) * mm, v(284.16, 387.16) * mm, v(281.01, 389.18) * mm, v(276.84, 389.18) * mm]});
            skFitSpline(sketch, "E240", {"points": [v(276.84, 389.18) * mm, v(274.08, 389.18) * mm, v(271.82, 388.38) * mm, v(270.07, 386.75) * mm]});
            skFitSpline(sketch, "E241", {"points": [v(270.07, 386.75) * mm, v(268.32, 385.12) * mm, v(267.44, 383.06) * mm, v(267.44, 380.56) * mm]});
            skFitSpline(sketch, "E242", {"points": [v(267.44, 380.56) * mm, v(267.44, 377.66) * mm, v(268.8, 375.02) * mm, v(271.5, 372.69) * mm]});
            skFitSpline(sketch, "E243", {"points": [v(271.5, 372.69) * mm, v(273.4, 373.18) * mm, v(275.11, 373.43) * mm, v(276.63, 373.43) * mm]});
            skFitSpline(sketch, "E244", {"points": [v(276.63, 373.43) * mm, v(278.07, 373.43) * mm, v(279.73, 373.08) * mm, v(281.63, 372.4) * mm]});
            skFitSpline(sketch, "E245", {"points": [v(281.63, 372.4) * mm, v(280.16, 367.34) * mm, v(277.58, 364.81) * mm, v(273.88, 364.81) * mm]});
            skFitSpline(sketch, "E246", {"points": [v(273.88, 364.81) * mm, v(272.36, 364.81) * mm, v(270.86, 365.22) * mm, v(269.35, 366.02) * mm]});
            skFitSpline(sketch, "E247", {"points": [v(269.35, 366.02) * mm, v(265.7, 364.5) * mm, v(262.72, 362.19) * mm, v(260.42, 359.13) * mm]});
            skFitSpline(sketch, "E248", {"points": [v(260.42, 359.13) * mm, v(258.12, 356.06) * mm, v(256.96, 352.8) * mm, v(256.96, 349.32) * mm]});
            skFitSpline(sketch, "E249", {"points": [v(256.96, 349.32) * mm, v(256.96, 346.25) * mm, v(258.1, 343.74) * mm, v(260.39, 341.8) * mm]});
            skFitSpline(sketch, "E250", {"points": [v(260.39, 341.8) * mm, v(262.67, 339.86) * mm, v(265.66, 338.88) * mm, v(269.4, 338.88) * mm]});
            skFitSpline(sketch, "E251", {"points": [v(269.4, 338.88) * mm, v(273.9, 338.88) * mm, v(278.46, 340.78) * mm, v(283.03, 344.56) * mm]});
            skFitSpline(sketch, "E252", {"points": [v(283.03, 344.56) * mm, v(287.61, 348.33) * mm, v(289.9, 352.03) * mm, v(289.9, 355.63) * mm]});
            skFitSpline(sketch, "E253", {"points": [v(289.9, 355.63) * mm, v(289.9, 357.33) * mm, v(289.16, 358.57) * mm, v(287.7, 359.33) * mm]});
            skFitSpline(sketch, "E254", {"points": [v(286.49, 359.8) * mm, v(285.1, 360.5) * mm, v(284.39, 361.54) * mm, v(284.39, 362.92) * mm]});
            skFitSpline(sketch, "E255", {"points": [v(284.39, 362.92) * mm, v(284.39, 364.24) * mm, v(284.98, 366.15) * mm, v(286.17, 368.6) * mm]});
            skFitSpline(sketch, "E256", {"points": [v(286.17, 368.6) * mm, v(289.42, 367.14) * mm, v(293.87, 366.41) * mm, v(299.52, 366.41) * mm]});
            skFitSpline(sketch, "E257", {"points": [v(299.52, 366.41) * mm, v(302.52, 366.41) * mm, v(305.82, 366.82) * mm, v(309.44, 367.62) * mm]});
            skFitSpline(sketch, "E258", {"points": [v(309.44, 367.62) * mm, v(308.5, 363.93) * mm, v(307.32, 361.5) * mm, v(305.9, 360.33) * mm]});
            skFitSpline(sketch, "E259", {"points": [v(305.9, 360.33) * mm, v(304.46, 359.17) * mm, v(302.3, 358.6) * mm, v(299.4, 358.6) * mm]});
            skFitSpline(sketch, "E260", {"points": [v(299.4, 358.6) * mm, v(298.84, 358.6) * mm, v(298.17, 358.64) * mm, v(297.4, 358.75) * mm]});
            skFitSpline(sketch, "E261", {"points": [v(297.4, 358.75) * mm, v(294.74, 350.17) * mm, v(293.41, 343.18) * mm, v(293.41, 337.77) * mm]});
            skFitSpline(sketch, "E262", {"points": [v(293.41, 337.77) * mm, v(293.41, 333.72) * mm, v(294.08, 330.44) * mm, v(295.4, 327.95) * mm]});
            skFitSpline(sketch, "E263", {"points": [v(295.4, 327.95) * mm, v(293.52, 325.82) * mm, v(291.53, 324.77) * mm, v(289.43, 324.77) * mm]});
            skFitSpline(sketch, "E264", {"points": [v(289.43, 324.77) * mm, v(287.44, 324.77) * mm, v(286.45, 326.37) * mm, v(286.45, 329.58) * mm]});
            skFitSpline(sketch, "E265", {"points": [v(286.45, 329.58) * mm, v(286.45, 332.7) * mm, v(287.06, 337.43) * mm, v(288.26, 343.75) * mm]});
            skFitSpline(sketch, "E266", {"points": [v(288.26, 343.75) * mm, v(282.52, 336.1) * mm, v(275.37, 332.25) * mm, v(266.85, 332.25) * mm]});
            skFitSpline(sketch, "E267", {"points": [v(266.85, 332.25) * mm, v(261.33, 332.25) * mm, v(256.9, 333.76) * mm, v(253.56, 336.78) * mm]});
            skFitSpline(sketch, "E268", {"points": [v(253.56, 336.78) * mm, v(250.21, 339.8) * mm, v(248.55, 343.84) * mm, v(248.55, 348.92) * mm]});
            skFitSpline(sketch, "E269", {"points": [v(248.55, 348.92) * mm, v(248.55, 358.85) * mm, v(254.08, 365.7) * mm, v(265.16, 369.52) * mm]});
            skFitSpline(sketch, "E270", {"points": [v(265.16, 369.52) * mm, v(261.45, 371.14) * mm, v(259.6, 374.46) * mm, v(259.6, 379.46) * mm]});
            skFitSpline(sketch, "E271", {"points": [v(259.6, 379.46) * mm, v(259.6, 383.85) * mm, v(261.34, 387.47) * mm, v(264.82, 390.34) * mm]});
            skFitSpline(sketch, "E272", {"points": [v(264.82, 390.34) * mm, v(268.3, 393.21) * mm, v(272.62, 394.65) * mm, v(277.79, 394.65) * mm]});
            skLineSegment(sketch, "E273", {"start": v(287.7, 359.33) * mm, "end": v(286.49, 359.8) * mm});
            skLineSegment(sketch, "E274", {"start": v(286.49, 359.8) * mm, "end": v(287.7, 359.33) * mm});
            skFitSpline(sketch, "E275", {"points": [v(277.79, 394.65) * mm, v(280.95, 394.65) * mm, v(283.67, 394.04) * mm, v(285.93, 392.83) * mm]});
            skFitSpline(sketch, "E276", {"points": [v(285.93, 392.83) * mm, v(288.2, 391.61) * mm, v(289.33, 390.05) * mm, v(289.33, 388.1) * mm]});
            skFitSpline(sketch, "E277", {"points": [v(289.33, 388.1) * mm, v(289.33, 386.55) * mm, v(288.3, 384.9) * mm, v(286.28, 383.13) * mm]});
            skFitSpline(sketch, "E278", {"points": [v(286.28, 383.13) * mm, v(284.16, 387.16) * mm, v(281.01, 389.18) * mm, v(276.84, 389.18) * mm]});
            skFitSpline(sketch, "E279", {"points": [v(276.84, 389.18) * mm, v(274.08, 389.18) * mm, v(271.82, 388.38) * mm, v(270.07, 386.75) * mm]});
            skFitSpline(sketch, "E280", {"points": [v(270.07, 386.75) * mm, v(268.32, 385.12) * mm, v(267.44, 383.06) * mm, v(267.44, 380.56) * mm]});
            skFitSpline(sketch, "E281", {"points": [v(267.44, 380.56) * mm, v(267.44, 377.66) * mm, v(268.8, 375.02) * mm, v(271.5, 372.69) * mm]});
            skFitSpline(sketch, "E282", {"points": [v(271.5, 372.69) * mm, v(273.4, 373.18) * mm, v(275.11, 373.43) * mm, v(276.63, 373.43) * mm]});
            skFitSpline(sketch, "E283", {"points": [v(276.63, 373.43) * mm, v(278.07, 373.43) * mm, v(279.73, 373.08) * mm, v(281.63, 372.4) * mm]});
            skFitSpline(sketch, "E284", {"points": [v(281.63, 372.4) * mm, v(280.16, 367.34) * mm, v(277.58, 364.81) * mm, v(273.88, 364.81) * mm]});
            skFitSpline(sketch, "E285", {"points": [v(273.88, 364.81) * mm, v(272.36, 364.81) * mm, v(270.86, 365.22) * mm, v(269.35, 366.02) * mm]});
            skFitSpline(sketch, "E286", {"points": [v(269.35, 366.02) * mm, v(265.7, 364.5) * mm, v(262.72, 362.19) * mm, v(260.42, 359.13) * mm]});
            skFitSpline(sketch, "E287", {"points": [v(260.42, 359.13) * mm, v(258.12, 356.06) * mm, v(256.96, 352.8) * mm, v(256.96, 349.32) * mm]});
            skFitSpline(sketch, "E288", {"points": [v(256.96, 349.32) * mm, v(256.96, 346.25) * mm, v(258.1, 343.74) * mm, v(260.39, 341.8) * mm]});
            skFitSpline(sketch, "E289", {"points": [v(260.39, 341.8) * mm, v(262.67, 339.86) * mm, v(265.66, 338.88) * mm, v(269.4, 338.88) * mm]});
            skFitSpline(sketch, "E290", {"points": [v(269.4, 338.88) * mm, v(273.9, 338.88) * mm, v(278.46, 340.78) * mm, v(283.03, 344.56) * mm]});
            skFitSpline(sketch, "E291", {"points": [v(283.03, 344.56) * mm, v(287.61, 348.33) * mm, v(289.9, 352.03) * mm, v(289.9, 355.63) * mm]});
            skFitSpline(sketch, "E292", {"points": [v(289.9, 355.63) * mm, v(289.9, 357.33) * mm, v(289.16, 358.57) * mm, v(287.7, 359.33) * mm]});
            skFitSpline(sketch, "E293", {"points": [v(286.49, 359.8) * mm, v(285.1, 360.5) * mm, v(284.39, 361.54) * mm, v(284.39, 362.92) * mm]});
            skFitSpline(sketch, "E294", {"points": [v(284.39, 362.92) * mm, v(284.39, 364.24) * mm, v(284.98, 366.15) * mm, v(286.17, 368.6) * mm]});
            skFitSpline(sketch, "E295", {"points": [v(286.17, 368.6) * mm, v(289.42, 367.14) * mm, v(293.87, 366.41) * mm, v(299.52, 366.41) * mm]});
            skFitSpline(sketch, "E296", {"points": [v(299.52, 366.41) * mm, v(302.52, 366.41) * mm, v(305.82, 366.82) * mm, v(309.44, 367.62) * mm]});
            skFitSpline(sketch, "E297", {"points": [v(309.44, 367.62) * mm, v(308.5, 363.93) * mm, v(307.32, 361.5) * mm, v(305.9, 360.33) * mm]});
            skFitSpline(sketch, "E298", {"points": [v(305.9, 360.33) * mm, v(304.46, 359.17) * mm, v(302.3, 358.6) * mm, v(299.4, 358.6) * mm]});
            skFitSpline(sketch, "E299", {"points": [v(299.4, 358.6) * mm, v(298.84, 358.6) * mm, v(298.17, 358.64) * mm, v(297.4, 358.75) * mm]});
            skFitSpline(sketch, "E300", {"points": [v(297.4, 358.75) * mm, v(294.74, 350.17) * mm, v(293.41, 343.18) * mm, v(293.41, 337.77) * mm]});
            skFitSpline(sketch, "E301", {"points": [v(293.41, 337.77) * mm, v(293.41, 333.72) * mm, v(294.08, 330.44) * mm, v(295.4, 327.95) * mm]});
            skFitSpline(sketch, "E302", {"points": [v(295.4, 327.95) * mm, v(293.52, 325.82) * mm, v(291.53, 324.77) * mm, v(289.43, 324.77) * mm]});
            skFitSpline(sketch, "E303", {"points": [v(289.43, 324.77) * mm, v(287.44, 324.77) * mm, v(286.45, 326.37) * mm, v(286.45, 329.58) * mm]});
            skFitSpline(sketch, "E304", {"points": [v(286.45, 329.58) * mm, v(286.45, 332.7) * mm, v(287.06, 337.43) * mm, v(288.26, 343.75) * mm]});
            skFitSpline(sketch, "E305", {"points": [v(288.26, 343.75) * mm, v(282.52, 336.1) * mm, v(275.37, 332.25) * mm, v(266.85, 332.25) * mm]});
            skFitSpline(sketch, "E306", {"points": [v(266.85, 332.25) * mm, v(261.33, 332.25) * mm, v(256.9, 333.76) * mm, v(253.56, 336.78) * mm]});
            skFitSpline(sketch, "E307", {"points": [v(253.56, 336.78) * mm, v(250.21, 339.8) * mm, v(248.55, 343.84) * mm, v(248.55, 348.92) * mm]});
            skFitSpline(sketch, "E308", {"points": [v(248.55, 348.92) * mm, v(248.55, 358.85) * mm, v(254.08, 365.7) * mm, v(265.16, 369.52) * mm]});
            skFitSpline(sketch, "E309", {"points": [v(265.16, 369.52) * mm, v(261.45, 371.14) * mm, v(259.6, 374.46) * mm, v(259.6, 379.46) * mm]});
            skFitSpline(sketch, "E310", {"points": [v(259.6, 379.46) * mm, v(259.6, 383.85) * mm, v(261.34, 387.47) * mm, v(264.82, 390.34) * mm]});
            skFitSpline(sketch, "E311", {"points": [v(264.82, 390.34) * mm, v(268.3, 393.21) * mm, v(272.62, 394.65) * mm, v(277.79, 394.65) * mm]});
            skFitSpline(sketch, "E312", {"points": [v(322.46, 256.65) * mm, v(318.75, 256.65) * mm, v(315.44, 254.74) * mm, v(312.52, 250.93) * mm]});
            skFitSpline(sketch, "E313", {"points": [v(312.52, 250.93) * mm, v(309.6, 247.1) * mm, v(308.14, 242.74) * mm, v(308.14, 237.81) * mm]});
            skFitSpline(sketch, "E314", {"points": [v(308.14, 237.81) * mm, v(308.14, 234.3) * mm, v(309, 231.42) * mm, v(310.71, 229.2) * mm]});
            skFitSpline(sketch, "E315", {"points": [v(310.71, 229.2) * mm, v(312.42, 227) * mm, v(314.6, 225.9) * mm, v(317.27, 225.9) * mm]});
            skFitSpline(sketch, "E316", {"points": [v(317.27, 225.9) * mm, v(320.96, 225.9) * mm, v(324.15, 228.04) * mm, v(326.87, 232.3) * mm]});
            skFitSpline(sketch, "E317", {"points": [v(326.87, 232.3) * mm, v(329.59, 236.57) * mm, v(330.95, 241.7) * mm, v(330.95, 247.66) * mm]});
            skFitSpline(sketch, "E318", {"points": [v(330.95, 247.66) * mm, v(330.95, 249.7) * mm, v(330.7, 251.56) * mm, v(330.2, 253.23) * mm]});
            skFitSpline(sketch, "E319", {"points": [v(330.2, 253.23) * mm, v(328.41, 253.83) * mm, v(326.72, 254.85) * mm, v(325.1, 256.27) * mm]});
            skFitSpline(sketch, "E320", {"points": [v(325.1, 256.27) * mm, v(324.07, 256.52) * mm, v(323.19, 256.65) * mm, v(322.46, 256.65) * mm]});
            skFitSpline(sketch, "E321", {"points": [v(240.42, 260.48) * mm, v(237.51, 260.48) * mm, v(234.78, 258.67) * mm, v(232.23, 255.02) * mm]});
            skFitSpline(sketch, "E322", {"points": [v(232.23, 255.02) * mm, v(229.66, 251.38) * mm, v(228.07, 247.23) * mm, v(227.45, 242.57) * mm]});
            skFitSpline(sketch, "E323", {"points": [v(227.45, 242.57) * mm, v(231.63, 242.83) * mm, v(235.4, 244.32) * mm, v(238.7, 247.04) * mm]});
            skFitSpline(sketch, "E324", {"points": [v(238.7, 247.04) * mm, v(242.03, 249.75) * mm, v(243.69, 252.82) * mm, v(243.69, 256.28) * mm]});
            skFitSpline(sketch, "E325", {"points": [v(243.69, 256.28) * mm, v(243.69, 259.09) * mm, v(242.6, 260.48) * mm, v(240.42, 260.48) * mm]});
            skFitSpline(sketch, "E326", {"points": [v(241.3, 265.95) * mm, v(244.47, 265.95) * mm, v(247.04, 265.03) * mm, v(249, 263.18) * mm]});
            skFitSpline(sketch, "E327", {"points": [v(249, 263.18) * mm, v(250.95, 261.35) * mm, v(251.93, 258.88) * mm, v(251.93, 255.8) * mm]});
            skFitSpline(sketch, "E328", {"points": [v(251.93, 255.8) * mm, v(251.93, 250.86) * mm, v(249.33, 246.53) * mm, v(244.16, 242.8) * mm]});
            skFitSpline(sketch, "E329", {"points": [v(244.16, 242.8) * mm, v(238.99, 239.07) * mm, v(233.32, 237.2) * mm, v(227.17, 237.2) * mm]});
            skFitSpline(sketch, "E330", {"points": [v(227.17, 237.2) * mm, v(227.17, 230.65) * mm, v(229.8, 227.37) * mm, v(235.06, 227.37) * mm]});
            skFitSpline(sketch, "E331", {"points": [v(235.06, 227.37) * mm, v(239.89, 227.37) * mm, v(245.25, 230) * mm, v(251.17, 235.25) * mm]});
            skFitSpline(sketch, "E332", {"points": [v(251.17, 235.25) * mm, v(256.88, 240.3) * mm, v(262.17, 247.06) * mm, v(267.04, 255.52) * mm]});
            skFitSpline(sketch, "E333", {"points": [v(267.04, 255.52) * mm, v(267.04, 255.63) * mm, v(267.05, 255.74) * mm, v(267.05, 255.84) * mm]});
            skFitSpline(sketch, "E334", {"points": [v(267.05, 255.84) * mm, v(267.05, 257.15) * mm, v(266.66, 258.53) * mm, v(265.9, 260) * mm]});
            skFitSpline(sketch, "E335", {"points": [v(265.9, 260) * mm, v(268.75, 261.23) * mm, v(270.96, 261.84) * mm, v(272.57, 261.84) * mm]});
            skFitSpline(sketch, "E336", {"points": [v(272.57, 261.84) * mm, v(274.69, 261.84) * mm, v(275.75, 260.41) * mm, v(275.75, 257.56) * mm]});
            skFitSpline(sketch, "E337", {"points": [v(275.75, 257.56) * mm, v(275.75, 256.1) * mm, v(275.15, 252.22) * mm, v(273.96, 245.95) * mm]});
            skFitSpline(sketch, "E338", {"points": [v(272.03, 235.67) * mm, v(275.54, 245) * mm, v(279.56, 252.4) * mm, v(284.1, 257.82) * mm]});
            skFitSpline(sketch, "E339", {"points": [v(284.1, 257.82) * mm, v(288.64, 263.24) * mm, v(292.83, 265.95) * mm, v(296.65, 265.95) * mm]});
            skFitSpline(sketch, "E340", {"points": [v(296.65, 265.95) * mm, v(298.1, 265.95) * mm, v(299.37, 265.46) * mm, v(300.46, 264.5) * mm]});
            skFitSpline(sketch, "E341", {"points": [v(300.46, 264.5) * mm, v(301.56, 263.54) * mm, v(302.1, 262.34) * mm, v(302.1, 260.93) * mm]});
            skFitSpline(sketch, "E342", {"points": [v(302.1, 260.93) * mm, v(302.1, 258.85) * mm, v(300, 256.15) * mm, v(295.8, 252.85) * mm]});
            skFitSpline(sketch, "E343", {"points": [v(295.8, 252.85) * mm, v(294.79, 254.9) * mm, v(293.62, 255.93) * mm, v(292.3, 255.93) * mm]});
            skFitSpline(sketch, "E344", {"points": [v(292.3, 255.93) * mm, v(289.6, 255.93) * mm, v(286.03, 252.53) * mm, v(281.6, 245.7) * mm]});
            skFitSpline(sketch, "E345", {"points": [v(281.6, 245.7) * mm, v(278.8, 241.39) * mm, v(276.38, 236.93) * mm, v(274.32, 232.34) * mm]});
            skFitSpline(sketch, "E346", {"points": [v(274.32, 232.34) * mm, v(272.26, 227.76) * mm, v(271.23, 224.47) * mm, v(271.23, 222.48) * mm]});
            skLineSegment(sketch, "E347", {"start": v(273.96, 245.95) * mm, "end": v(272.83, 239.95) * mm});
            skLineSegment(sketch, "E348", {"start": v(272.83, 239.95) * mm, "end": v(273.96, 245.95) * mm});
            skFitSpline(sketch, "E349", {"points": [v(271.27, 221.52) * mm, v(269.31, 220.47) * mm, v(267.8, 219.95) * mm, v(266.72, 219.95) * mm]});
            skFitSpline(sketch, "E350", {"points": [v(266.72, 219.95) * mm, v(263.89, 219.95) * mm, v(262.46, 221.4) * mm, v(262.46, 224.27) * mm]});
            skFitSpline(sketch, "E351", {"points": [v(262.46, 224.27) * mm, v(262.46, 225.52) * mm, v(262.89, 228.56) * mm, v(263.72, 233.37) * mm]});
            skLineSegment(sketch, "E352", {"start": v(271.23, 222.48) * mm, "end": v(271.27, 221.52) * mm});
            skLineSegment(sketch, "E353", {"start": v(271.27, 221.52) * mm, "end": v(271.23, 222.48) * mm});
            skFitSpline(sketch, "E354", {"points": [v(265.47, 243.21) * mm, v(261.99, 237.94) * mm, v(257.98, 233.36) * mm, v(253.47, 229.48) * mm]});
            skFitSpline(sketch, "E355", {"points": [v(253.47, 229.48) * mm, v(246.07, 223.13) * mm, v(239.03, 219.95) * mm, v(232.34, 219.95) * mm]});
            skFitSpline(sketch, "E356", {"points": [v(232.34, 219.95) * mm, v(227.94, 219.95) * mm, v(224.47, 221.55) * mm, v(221.91, 224.73) * mm]});
            skFitSpline(sketch, "E357", {"points": [v(221.91, 224.73) * mm, v(219.35, 227.92) * mm, v(218.07, 232.24) * mm, v(218.07, 237.69) * mm]});
            skFitSpline(sketch, "E358", {"points": [v(218.07, 237.69) * mm, v(218.07, 245.46) * mm, v(220.34, 252.12) * mm, v(224.87, 257.65) * mm]});
            skFitSpline(sketch, "E359", {"points": [v(224.87, 257.65) * mm, v(229.4, 263.18) * mm, v(234.88, 265.95) * mm, v(241.3, 265.95) * mm]});
            skLineSegment(sketch, "E360", {"start": v(265.13, 241.29) * mm, "end": v(263.72, 233.37) * mm});
            skFitSpline(sketch, "E361", {"points": [v(321.7, 268.35) * mm, v(327.88, 267.8) * mm, v(332.88, 264.45) * mm, v(336.73, 258.33) * mm]});
            skFitSpline(sketch, "E362", {"points": [v(336.73, 258.33) * mm, v(340.37, 255.54) * mm, v(344.2, 254.14) * mm, v(348.24, 254.14) * mm]});
            skFitSpline(sketch, "E363", {"points": [v(348.24, 254.14) * mm, v(349.7, 254.14) * mm, v(351.28, 254.46) * mm, v(353, 255.14) * mm]});
            skFitSpline(sketch, "E364", {"points": [v(353, 255.14) * mm, v(352.25, 256.33) * mm, v(351.5, 257.44) * mm, v(350.72, 258.45) * mm]});
            skFitSpline(sketch, "E365", {"points": [v(350.72, 258.45) * mm, v(352.74, 260.55) * mm, v(354.74, 261.6) * mm, v(356.73, 261.6) * mm]});
            skFitSpline(sketch, "E366", {"points": [v(356.73, 261.6) * mm, v(358.54, 261.6) * mm, v(360, 260.73) * mm, v(361.14, 259) * mm]});
            skFitSpline(sketch, "E367", {"points": [v(361.14, 259) * mm, v(362.27, 257.26) * mm, v(363.63, 254) * mm, v(365.2, 249.2) * mm]});
            skFitSpline(sketch, "E368", {"points": [v(365.2, 249.2) * mm, v(367.64, 241.7) * mm, v(369.34, 235.1) * mm, v(370.3, 229.37) * mm]});
            skFitSpline(sketch, "E369", {"points": [v(370.3, 229.37) * mm, v(377.47, 242.97) * mm, v(381.38, 255.16) * mm, v(382.06, 265.95) * mm]});
            skFitSpline(sketch, "E370", {"points": [v(382.06, 265.95) * mm, v(387.06, 265.2) * mm, v(389.57, 263.4) * mm, v(389.57, 260.57) * mm]});
            skFitSpline(sketch, "E371", {"points": [v(389.57, 260.57) * mm, v(389.57, 257.95) * mm, v(387.72, 252.7) * mm, v(384.02, 244.83) * mm]});
            skFitSpline(sketch, "E372", {"points": [v(384.02, 244.83) * mm, v(380.32, 236.96) * mm, v(376.35, 229.75) * mm, v(372.1, 223.22) * mm]});
            skFitSpline(sketch, "E373", {"points": [v(372.1, 223.22) * mm, v(367.2, 215.7) * mm, v(362.28, 209.74) * mm, v(357.38, 205.33) * mm]});
            skFitSpline(sketch, "E374", {"points": [v(357.38, 205.33) * mm, v(352.47, 200.93) * mm, v(348.2, 198.73) * mm, v(344.57, 198.73) * mm]});
            skFitSpline(sketch, "E375", {"points": [v(344.57, 198.73) * mm, v(340.98, 198.73) * mm, v(339.18, 200.47) * mm, v(339.18, 203.94) * mm]});
            skFitSpline(sketch, "E376", {"points": [v(339.18, 203.94) * mm, v(339.18, 205.24) * mm, v(339.59, 206.91) * mm, v(340.38, 208.95) * mm]});
            skFitSpline(sketch, "E377", {"points": [v(340.38, 208.95) * mm, v(342.03, 208.07) * mm, v(343.73, 207.63) * mm, v(345.47, 207.63) * mm]});
            skFitSpline(sketch, "E378", {"points": [v(345.47, 207.63) * mm, v(352.03, 207.63) * mm, v(358.3, 212.46) * mm, v(364.27, 222.14) * mm]});
            skFitSpline(sketch, "E379", {"points": [v(364.27, 222.14) * mm, v(363.28, 228.86) * mm, v(361.54, 235.6) * mm, v(359.02, 242.38) * mm]});
            skFitSpline(sketch, "E380", {"points": [v(359.02, 242.38) * mm, v(357.95, 245.25) * mm, v(356.83, 247.88) * mm, v(355.67, 250.25) * mm]});
            skFitSpline(sketch, "E381", {"points": [v(355.67, 250.25) * mm, v(352.93, 248.72) * mm, v(350.19, 247.96) * mm, v(347.44, 247.96) * mm]});
            skFitSpline(sketch, "E382", {"points": [v(347.44, 247.96) * mm, v(344.78, 247.96) * mm, v(342.1, 248.56) * mm, v(339.4, 249.76) * mm]});
            skFitSpline(sketch, "E383", {"points": [v(339.4, 249.76) * mm, v(339.48, 249.66) * mm, v(339.5, 249.36) * mm, v(339.5, 248.87) * mm]});
            skFitSpline(sketch, "E384", {"points": [v(339.5, 248.87) * mm, v(339.5, 241.14) * mm, v(337.16, 234.38) * mm, v(332.49, 228.6) * mm]});
            skFitSpline(sketch, "E385", {"points": [v(332.49, 228.6) * mm, v(327.8, 222.83) * mm, v(322.3, 219.95) * mm, v(315.95, 219.95) * mm]});
            skFitSpline(sketch, "E386", {"points": [v(315.95, 219.95) * mm, v(311.1, 219.95) * mm, v(307.12, 221.7) * mm, v(304.05, 225.22) * mm]});
            skFitSpline(sketch, "E387", {"points": [v(304.05, 225.22) * mm, v(300.98, 228.72) * mm, v(299.44, 233.26) * mm, v(299.44, 238.82) * mm]});
            skFitSpline(sketch, "E388", {"points": [v(299.44, 238.82) * mm, v(299.44, 245.12) * mm, v(301.4, 250.58) * mm, v(305.33, 255.2) * mm]});
            skFitSpline(sketch, "E389", {"points": [v(305.33, 255.2) * mm, v(309.26, 259.81) * mm, v(313.9, 262.12) * mm, v(319.26, 262.12) * mm]});
            skFitSpline(sketch, "E390", {"points": [v(319.26, 262.12) * mm, v(320.1, 262.12) * mm, v(320.7, 262) * mm, v(321.06, 261.76) * mm]});
            skFitSpline(sketch, "E391", {"points": [v(321.06, 261.76) * mm, v(320.47, 262.26) * mm, v(320.19, 263) * mm, v(320.19, 263.94) * mm]});
            skFitSpline(sketch, "E392", {"points": [v(320.19, 263.94) * mm, v(320.19, 265.37) * mm, v(320.7, 266.85) * mm, v(321.7, 268.35) * mm]});
            skFitSpline(sketch, "E393", {"points": [v(190.94, 286.25) * mm, v(192.87, 286.25) * mm, v(193.84, 285.06) * mm, v(193.84, 282.68) * mm]});
            skFitSpline(sketch, "E394", {"points": [v(193.84, 282.68) * mm, v(193.84, 282.18) * mm, v(193.44, 279.75) * mm, v(192.63, 275.4) * mm]});
            skFitSpline(sketch, "E395", {"points": [v(186.62, 241.34) * mm, v(185.75, 236.5) * mm, v(185.32, 233.12) * mm, v(185.32, 231.22) * mm]});
            skFitSpline(sketch, "E396", {"points": [v(185.32, 231.22) * mm, v(185.32, 228.5) * mm, v(188.28, 227.13) * mm, v(194.21, 227.13) * mm]});
            skFitSpline(sketch, "E397", {"points": [v(194.21, 227.13) * mm, v(199.86, 227.13) * mm, v(206.02, 228.45) * mm, v(212.68, 231.08) * mm]});
            skFitSpline(sketch, "E398", {"points": [v(212.68, 231.08) * mm, v(211.84, 227.71) * mm, v(210.86, 225.39) * mm, v(209.73, 224.13) * mm]});
            skFitSpline(sketch, "E399", {"points": [v(209.73, 224.13) * mm, v(208.6, 222.84) * mm, v(205.85, 221.75) * mm, v(201.5, 220.86) * mm]});
            skFitSpline(sketch, "E400", {"points": [v(201.5, 220.86) * mm, v(197.16, 219.96) * mm, v(192.62, 219.5) * mm, v(187.87, 219.5) * mm]});
            skFitSpline(sketch, "E401", {"points": [v(187.87, 219.5) * mm, v(179.99, 219.5) * mm, v(176.05, 222.62) * mm, v(176.05, 228.83) * mm]});
            skFitSpline(sketch, "E402", {"points": [v(176.05, 228.83) * mm, v(176.05, 230.48) * mm, v(176.44, 233.54) * mm, v(177.24, 238.01) * mm]});
            skLineSegment(sketch, "E403", {"start": v(192.63, 275.4) * mm, "end": v(186.62, 241.34) * mm});
            skLineSegment(sketch, "E404", {"start": v(186.62, 241.34) * mm, "end": v(192.63, 275.4) * mm});
            skFitSpline(sketch, "E405", {"points": [v(184.03, 276.41) * mm, v(184.41, 278.6) * mm, v(184.6, 280.13) * mm, v(184.6, 281.03) * mm]});
            skFitSpline(sketch, "E406", {"points": [v(184.6, 281.03) * mm, v(184.6, 281.73) * mm, v(184.33, 282.67) * mm, v(183.79, 283.85) * mm]});
            skFitSpline(sketch, "E407", {"points": [v(183.79, 283.85) * mm, v(187.28, 285.45) * mm, v(189.66, 286.25) * mm, v(190.94, 286.25) * mm]});
            skLineSegment(sketch, "E408", {"start": v(177.24, 238.01) * mm, "end": v(184.03, 276.41) * mm});
            skLineSegment(sketch, "E409", {"start": v(184.03, 276.41) * mm, "end": v(177.24, 238.01) * mm});
            skFitSpline(sketch, "E410", {"points": [v(322.46, 256.65) * mm, v(318.75, 256.65) * mm, v(315.44, 254.74) * mm, v(312.52, 250.93) * mm]});
            skFitSpline(sketch, "E411", {"points": [v(312.52, 250.93) * mm, v(309.6, 247.1) * mm, v(308.14, 242.74) * mm, v(308.14, 237.81) * mm]});
            skFitSpline(sketch, "E412", {"points": [v(308.14, 237.81) * mm, v(308.14, 234.3) * mm, v(309, 231.42) * mm, v(310.71, 229.2) * mm]});
            skFitSpline(sketch, "E413", {"points": [v(310.71, 229.2) * mm, v(312.42, 227) * mm, v(314.6, 225.9) * mm, v(317.27, 225.9) * mm]});
            skFitSpline(sketch, "E414", {"points": [v(317.27, 225.9) * mm, v(320.96, 225.9) * mm, v(324.15, 228.04) * mm, v(326.87, 232.3) * mm]});
            skFitSpline(sketch, "E415", {"points": [v(326.87, 232.3) * mm, v(329.59, 236.57) * mm, v(330.95, 241.7) * mm, v(330.95, 247.66) * mm]});
            skFitSpline(sketch, "E416", {"points": [v(330.95, 247.66) * mm, v(330.95, 249.7) * mm, v(330.7, 251.56) * mm, v(330.2, 253.23) * mm]});
            skFitSpline(sketch, "E417", {"points": [v(330.2, 253.23) * mm, v(328.41, 253.83) * mm, v(326.72, 254.85) * mm, v(325.1, 256.27) * mm]});
            skFitSpline(sketch, "E418", {"points": [v(325.1, 256.27) * mm, v(324.07, 256.52) * mm, v(323.19, 256.65) * mm, v(322.46, 256.65) * mm]});
            skFitSpline(sketch, "E419", {"points": [v(240.42, 260.48) * mm, v(237.51, 260.48) * mm, v(234.78, 258.67) * mm, v(232.23, 255.02) * mm]});
            skFitSpline(sketch, "E420", {"points": [v(232.23, 255.02) * mm, v(229.66, 251.38) * mm, v(228.07, 247.23) * mm, v(227.45, 242.57) * mm]});
            skFitSpline(sketch, "E421", {"points": [v(227.45, 242.57) * mm, v(231.63, 242.83) * mm, v(235.4, 244.32) * mm, v(238.7, 247.04) * mm]});
            skFitSpline(sketch, "E422", {"points": [v(238.7, 247.04) * mm, v(242.03, 249.75) * mm, v(243.69, 252.82) * mm, v(243.69, 256.28) * mm]});
            skFitSpline(sketch, "E423", {"points": [v(243.69, 256.28) * mm, v(243.69, 259.09) * mm, v(242.6, 260.48) * mm, v(240.42, 260.48) * mm]});
            skFitSpline(sketch, "E424", {"points": [v(241.3, 265.95) * mm, v(244.47, 265.95) * mm, v(247.04, 265.03) * mm, v(249, 263.18) * mm]});
            skFitSpline(sketch, "E425", {"points": [v(249, 263.18) * mm, v(250.95, 261.35) * mm, v(251.93, 258.88) * mm, v(251.93, 255.8) * mm]});
            skFitSpline(sketch, "E426", {"points": [v(251.93, 255.8) * mm, v(251.93, 250.86) * mm, v(249.33, 246.53) * mm, v(244.16, 242.8) * mm]});
            skFitSpline(sketch, "E427", {"points": [v(244.16, 242.8) * mm, v(238.99, 239.07) * mm, v(233.32, 237.2) * mm, v(227.17, 237.2) * mm]});
            skFitSpline(sketch, "E428", {"points": [v(227.17, 237.2) * mm, v(227.17, 230.65) * mm, v(229.8, 227.37) * mm, v(235.06, 227.37) * mm]});
            skFitSpline(sketch, "E429", {"points": [v(235.06, 227.37) * mm, v(239.89, 227.37) * mm, v(245.25, 230) * mm, v(251.17, 235.25) * mm]});
            skFitSpline(sketch, "E430", {"points": [v(251.17, 235.25) * mm, v(256.88, 240.3) * mm, v(262.17, 247.06) * mm, v(267.04, 255.52) * mm]});
            skFitSpline(sketch, "E431", {"points": [v(267.04, 255.52) * mm, v(267.04, 255.63) * mm, v(267.05, 255.74) * mm, v(267.05, 255.84) * mm]});
            skFitSpline(sketch, "E432", {"points": [v(267.05, 255.84) * mm, v(267.05, 257.15) * mm, v(266.66, 258.53) * mm, v(265.9, 260) * mm]});
            skFitSpline(sketch, "E433", {"points": [v(265.9, 260) * mm, v(268.75, 261.23) * mm, v(270.96, 261.84) * mm, v(272.57, 261.84) * mm]});
            skFitSpline(sketch, "E434", {"points": [v(272.57, 261.84) * mm, v(274.69, 261.84) * mm, v(275.75, 260.41) * mm, v(275.75, 257.56) * mm]});
            skFitSpline(sketch, "E435", {"points": [v(275.75, 257.56) * mm, v(275.75, 256.1) * mm, v(275.15, 252.22) * mm, v(273.96, 245.95) * mm]});
            skFitSpline(sketch, "E436", {"points": [v(272.03, 235.67) * mm, v(275.54, 245) * mm, v(279.56, 252.4) * mm, v(284.1, 257.82) * mm]});
            skFitSpline(sketch, "E437", {"points": [v(284.1, 257.82) * mm, v(288.64, 263.24) * mm, v(292.83, 265.95) * mm, v(296.65, 265.95) * mm]});
            skFitSpline(sketch, "E438", {"points": [v(296.65, 265.95) * mm, v(298.1, 265.95) * mm, v(299.37, 265.46) * mm, v(300.46, 264.5) * mm]});
            skFitSpline(sketch, "E439", {"points": [v(300.46, 264.5) * mm, v(301.56, 263.54) * mm, v(302.1, 262.34) * mm, v(302.1, 260.93) * mm]});
            skFitSpline(sketch, "E440", {"points": [v(302.1, 260.93) * mm, v(302.1, 258.85) * mm, v(300, 256.15) * mm, v(295.8, 252.85) * mm]});
            skFitSpline(sketch, "E441", {"points": [v(295.8, 252.85) * mm, v(294.79, 254.9) * mm, v(293.62, 255.93) * mm, v(292.3, 255.93) * mm]});
            skFitSpline(sketch, "E442", {"points": [v(292.3, 255.93) * mm, v(289.6, 255.93) * mm, v(286.03, 252.53) * mm, v(281.6, 245.7) * mm]});
            skFitSpline(sketch, "E443", {"points": [v(281.6, 245.7) * mm, v(278.8, 241.39) * mm, v(276.38, 236.93) * mm, v(274.32, 232.34) * mm]});
            skFitSpline(sketch, "E444", {"points": [v(274.32, 232.34) * mm, v(272.26, 227.76) * mm, v(271.23, 224.47) * mm, v(271.23, 222.48) * mm]});
            skFitSpline(sketch, "E445", {"points": [v(271.27, 221.52) * mm, v(269.31, 220.47) * mm, v(267.8, 219.95) * mm, v(266.72, 219.95) * mm]});
            skFitSpline(sketch, "E446", {"points": [v(266.72, 219.95) * mm, v(263.89, 219.95) * mm, v(262.46, 221.4) * mm, v(262.46, 224.27) * mm]});
            skFitSpline(sketch, "E447", {"points": [v(262.46, 224.27) * mm, v(262.46, 225.52) * mm, v(262.89, 228.56) * mm, v(263.72, 233.37) * mm]});
            skFitSpline(sketch, "E448", {"points": [v(265.47, 243.21) * mm, v(261.99, 237.94) * mm, v(257.98, 233.36) * mm, v(253.47, 229.48) * mm]});
            skFitSpline(sketch, "E449", {"points": [v(253.47, 229.48) * mm, v(246.07, 223.13) * mm, v(239.03, 219.95) * mm, v(232.34, 219.95) * mm]});
            skFitSpline(sketch, "E450", {"points": [v(232.34, 219.95) * mm, v(227.94, 219.95) * mm, v(224.47, 221.55) * mm, v(221.91, 224.73) * mm]});
            skFitSpline(sketch, "E451", {"points": [v(221.91, 224.73) * mm, v(219.35, 227.92) * mm, v(218.07, 232.24) * mm, v(218.07, 237.69) * mm]});
            skFitSpline(sketch, "E452", {"points": [v(218.07, 237.69) * mm, v(218.07, 245.46) * mm, v(220.34, 252.12) * mm, v(224.87, 257.65) * mm]});
            skFitSpline(sketch, "E453", {"points": [v(224.87, 257.65) * mm, v(229.4, 263.18) * mm, v(234.88, 265.95) * mm, v(241.3, 265.95) * mm]});
            skFitSpline(sketch, "E454", {"points": [v(321.7, 268.35) * mm, v(327.88, 267.8) * mm, v(332.88, 264.45) * mm, v(336.73, 258.33) * mm]});
            skFitSpline(sketch, "E455", {"points": [v(336.73, 258.33) * mm, v(340.37, 255.54) * mm, v(344.2, 254.14) * mm, v(348.24, 254.14) * mm]});
            skFitSpline(sketch, "E456", {"points": [v(348.24, 254.14) * mm, v(349.7, 254.14) * mm, v(351.28, 254.46) * mm, v(353, 255.14) * mm]});
            skFitSpline(sketch, "E457", {"points": [v(353, 255.14) * mm, v(352.25, 256.33) * mm, v(351.5, 257.44) * mm, v(350.72, 258.45) * mm]});
            skFitSpline(sketch, "E458", {"points": [v(350.72, 258.45) * mm, v(352.74, 260.55) * mm, v(354.74, 261.6) * mm, v(356.73, 261.6) * mm]});
            skFitSpline(sketch, "E459", {"points": [v(356.73, 261.6) * mm, v(358.54, 261.6) * mm, v(360, 260.73) * mm, v(361.14, 259) * mm]});
            skFitSpline(sketch, "E460", {"points": [v(361.14, 259) * mm, v(362.27, 257.26) * mm, v(363.63, 254) * mm, v(365.2, 249.2) * mm]});
            skFitSpline(sketch, "E461", {"points": [v(365.2, 249.2) * mm, v(367.64, 241.7) * mm, v(369.34, 235.1) * mm, v(370.3, 229.37) * mm]});
            skFitSpline(sketch, "E462", {"points": [v(370.3, 229.37) * mm, v(377.47, 242.97) * mm, v(381.38, 255.16) * mm, v(382.06, 265.95) * mm]});
            skFitSpline(sketch, "E463", {"points": [v(382.06, 265.95) * mm, v(387.06, 265.2) * mm, v(389.57, 263.4) * mm, v(389.57, 260.57) * mm]});
            skFitSpline(sketch, "E464", {"points": [v(389.57, 260.57) * mm, v(389.57, 257.95) * mm, v(387.72, 252.7) * mm, v(384.02, 244.83) * mm]});
            skFitSpline(sketch, "E465", {"points": [v(384.02, 244.83) * mm, v(380.32, 236.96) * mm, v(376.35, 229.75) * mm, v(372.1, 223.22) * mm]});
            skFitSpline(sketch, "E466", {"points": [v(372.1, 223.22) * mm, v(367.2, 215.7) * mm, v(362.28, 209.74) * mm, v(357.38, 205.33) * mm]});
            skFitSpline(sketch, "E467", {"points": [v(357.38, 205.33) * mm, v(352.47, 200.93) * mm, v(348.2, 198.73) * mm, v(344.57, 198.73) * mm]});
            skFitSpline(sketch, "E468", {"points": [v(344.57, 198.73) * mm, v(340.98, 198.73) * mm, v(339.18, 200.47) * mm, v(339.18, 203.94) * mm]});
            skFitSpline(sketch, "E469", {"points": [v(339.18, 203.94) * mm, v(339.18, 205.24) * mm, v(339.59, 206.91) * mm, v(340.38, 208.95) * mm]});
            skFitSpline(sketch, "E470", {"points": [v(340.38, 208.95) * mm, v(342.03, 208.07) * mm, v(343.73, 207.63) * mm, v(345.47, 207.63) * mm]});
            skFitSpline(sketch, "E471", {"points": [v(345.47, 207.63) * mm, v(352.03, 207.63) * mm, v(358.3, 212.46) * mm, v(364.27, 222.14) * mm]});
            skFitSpline(sketch, "E472", {"points": [v(364.27, 222.14) * mm, v(363.28, 228.86) * mm, v(361.54, 235.6) * mm, v(359.02, 242.38) * mm]});
            skFitSpline(sketch, "E473", {"points": [v(359.02, 242.38) * mm, v(357.95, 245.25) * mm, v(356.83, 247.88) * mm, v(355.67, 250.25) * mm]});
            skFitSpline(sketch, "E474", {"points": [v(355.67, 250.25) * mm, v(352.93, 248.72) * mm, v(350.19, 247.96) * mm, v(347.44, 247.96) * mm]});
            skFitSpline(sketch, "E475", {"points": [v(347.44, 247.96) * mm, v(344.78, 247.96) * mm, v(342.1, 248.56) * mm, v(339.4, 249.76) * mm]});
            skFitSpline(sketch, "E476", {"points": [v(339.4, 249.76) * mm, v(339.48, 249.66) * mm, v(339.5, 249.36) * mm, v(339.5, 248.87) * mm]});
            skFitSpline(sketch, "E477", {"points": [v(339.5, 248.87) * mm, v(339.5, 241.14) * mm, v(337.16, 234.38) * mm, v(332.49, 228.6) * mm]});
            skFitSpline(sketch, "E478", {"points": [v(332.49, 228.6) * mm, v(327.8, 222.83) * mm, v(322.3, 219.95) * mm, v(315.95, 219.95) * mm]});
            skFitSpline(sketch, "E479", {"points": [v(315.95, 219.95) * mm, v(311.1, 219.95) * mm, v(307.12, 221.7) * mm, v(304.05, 225.22) * mm]});
            skFitSpline(sketch, "E480", {"points": [v(304.05, 225.22) * mm, v(300.98, 228.72) * mm, v(299.44, 233.26) * mm, v(299.44, 238.82) * mm]});
            skFitSpline(sketch, "E481", {"points": [v(299.44, 238.82) * mm, v(299.44, 245.12) * mm, v(301.4, 250.58) * mm, v(305.33, 255.2) * mm]});
            skFitSpline(sketch, "E482", {"points": [v(305.33, 255.2) * mm, v(309.26, 259.81) * mm, v(313.9, 262.12) * mm, v(319.26, 262.12) * mm]});
            skFitSpline(sketch, "E483", {"points": [v(319.26, 262.12) * mm, v(320.1, 262.12) * mm, v(320.7, 262) * mm, v(321.06, 261.76) * mm]});
            skFitSpline(sketch, "E484", {"points": [v(321.06, 261.76) * mm, v(320.47, 262.26) * mm, v(320.19, 263) * mm, v(320.19, 263.94) * mm]});
            skFitSpline(sketch, "E485", {"points": [v(320.19, 263.94) * mm, v(320.19, 265.37) * mm, v(320.7, 266.85) * mm, v(321.7, 268.35) * mm]});
            skFitSpline(sketch, "E486", {"points": [v(190.94, 286.25) * mm, v(192.87, 286.25) * mm, v(193.84, 285.06) * mm, v(193.84, 282.68) * mm]});
            skFitSpline(sketch, "E487", {"points": [v(193.84, 282.68) * mm, v(193.84, 282.18) * mm, v(193.44, 279.75) * mm, v(192.63, 275.4) * mm]});
            skFitSpline(sketch, "E488", {"points": [v(186.62, 241.34) * mm, v(185.75, 236.5) * mm, v(185.32, 233.12) * mm, v(185.32, 231.22) * mm]});
            skFitSpline(sketch, "E489", {"points": [v(185.32, 231.22) * mm, v(185.32, 228.5) * mm, v(188.28, 227.13) * mm, v(194.21, 227.13) * mm]});
            skFitSpline(sketch, "E490", {"points": [v(194.21, 227.13) * mm, v(199.86, 227.13) * mm, v(206.02, 228.45) * mm, v(212.68, 231.08) * mm]});
            skFitSpline(sketch, "E491", {"points": [v(212.68, 231.08) * mm, v(211.84, 227.71) * mm, v(210.86, 225.39) * mm, v(209.73, 224.13) * mm]});
            skFitSpline(sketch, "E492", {"points": [v(209.73, 224.13) * mm, v(208.6, 222.84) * mm, v(205.85, 221.75) * mm, v(201.5, 220.86) * mm]});
            skFitSpline(sketch, "E493", {"points": [v(201.5, 220.86) * mm, v(197.16, 219.96) * mm, v(192.62, 219.5) * mm, v(187.87, 219.5) * mm]});
            skFitSpline(sketch, "E494", {"points": [v(187.87, 219.5) * mm, v(179.99, 219.5) * mm, v(176.05, 222.62) * mm, v(176.05, 228.83) * mm]});
            skFitSpline(sketch, "E495", {"points": [v(176.05, 228.83) * mm, v(176.05, 230.48) * mm, v(176.44, 233.54) * mm, v(177.24, 238.01) * mm]});
            skFitSpline(sketch, "E496", {"points": [v(184.03, 276.41) * mm, v(184.41, 278.6) * mm, v(184.6, 280.13) * mm, v(184.6, 281.03) * mm]});
            skFitSpline(sketch, "E497", {"points": [v(184.6, 281.03) * mm, v(184.6, 281.73) * mm, v(184.33, 282.67) * mm, v(183.79, 283.85) * mm]});
            skFitSpline(sketch, "E498", {"points": [v(183.79, 283.85) * mm, v(187.28, 285.45) * mm, v(189.66, 286.25) * mm, v(190.94, 286.25) * mm]});
            skFitSpline(sketch, "E499", {"points": [v(148.9, 160.76) * mm, v(152.84, 160.76) * mm, v(156.03, 159.69) * mm, v(158.5, 157.52) * mm]});
            skFitSpline(sketch, "E500", {"points": [v(158.5, 157.52) * mm, v(160.96, 155.36) * mm, v(162.2, 152.5) * mm, v(162.2, 148.95) * mm]});
            skFitSpline(sketch, "E501", {"points": [v(162.2, 148.95) * mm, v(162.2, 139.05) * mm, v(152.73, 125.67) * mm, v(133.82, 108.83) * mm]});
            skFitSpline(sketch, "E502", {"points": [v(133.82, 108.83) * mm, v(141.2, 110.02) * mm, v(147.51, 110.62) * mm, v(152.72, 110.62) * mm]});
            skFitSpline(sketch, "E503", {"points": [v(152.72, 110.62) * mm, v(156.78, 110.62) * mm, v(159.46, 109.94) * mm, v(160.79, 108.57) * mm]});
            skFitSpline(sketch, "E504", {"points": [v(160.79, 108.57) * mm, v(162.11, 107.2) * mm, v(162.93, 103.95) * mm, v(163.25, 98.82) * mm]});
            skFitSpline(sketch, "E505", {"points": [v(163.25, 98.82) * mm, v(159.1, 100.65) * mm, v(154.02, 101.57) * mm, v(148.06, 101.57) * mm]});
            skFitSpline(sketch, "E506", {"points": [v(148.06, 101.57) * mm, v(143.16, 101.57) * mm, v(138.24, 101.13) * mm, v(133.32, 100.27) * mm]});
            skFitSpline(sketch, "E507", {"points": [v(131.2, 99.92) * mm, v(129.2, 99.58) * mm, v(127.89, 99.4) * mm, v(127.26, 99.4) * mm]});
            skFitSpline(sketch, "E508", {"points": [v(127.26, 99.4) * mm, v(125.1, 99.4) * mm, v(124.04, 100.8) * mm, v(124.04, 103.6) * mm]});
            skFitSpline(sketch, "E509", {"points": [v(124.04, 103.6) * mm, v(124.04, 104.4) * mm, v(124.14, 105.62) * mm, v(124.32, 107.24) * mm]});
            skFitSpline(sketch, "E510", {"points": [v(124.32, 107.24) * mm, v(132.32, 113.12) * mm, v(139.12, 119.9) * mm, v(144.71, 127.63) * mm]});
            skFitSpline(sketch, "E511", {"points": [v(144.71, 127.63) * mm, v(150.3, 135.35) * mm, v(153.1, 141.66) * mm, v(153.1, 146.57) * mm]});
            skFitSpline(sketch, "E512", {"points": [v(153.1, 146.57) * mm, v(153.1, 151.09) * mm, v(150.85, 153.34) * mm, v(146.35, 153.34) * mm]});
            skFitSpline(sketch, "E513", {"points": [v(146.35, 153.34) * mm, v(140.98, 153.34) * mm, v(135.91, 149.75) * mm, v(131.13, 142.53) * mm]});
            skFitSpline(sketch, "E514", {"points": [v(131.13, 142.53) * mm, v(130.6, 144.51) * mm, v(130.34, 146) * mm, v(130.34, 147.01) * mm]});
            skFitSpline(sketch, "E515", {"points": [v(130.34, 147.01) * mm, v(130.34, 150.43) * mm, v(132.32, 153.57) * mm, v(136.28, 156.45) * mm]});
            skFitSpline(sketch, "E516", {"points": [v(136.28, 156.45) * mm, v(140.24, 159.33) * mm, v(144.45, 160.76) * mm, v(148.9, 160.76) * mm]});
            skLineSegment(sketch, "E517", {"start": v(133.32, 100.27) * mm, "end": v(131.2, 99.92) * mm});
            skLineSegment(sketch, "E518", {"start": v(131.2, 99.92) * mm, "end": v(133.32, 100.27) * mm});
            skFitSpline(sketch, "E519", {"points": [v(148.9, 160.76) * mm, v(152.84, 160.76) * mm, v(156.03, 159.69) * mm, v(158.5, 157.52) * mm]});
            skFitSpline(sketch, "E520", {"points": [v(158.5, 157.52) * mm, v(160.96, 155.36) * mm, v(162.2, 152.5) * mm, v(162.2, 148.95) * mm]});
            skFitSpline(sketch, "E521", {"points": [v(162.2, 148.95) * mm, v(162.2, 139.05) * mm, v(152.73, 125.67) * mm, v(133.82, 108.83) * mm]});
            skFitSpline(sketch, "E522", {"points": [v(133.82, 108.83) * mm, v(141.2, 110.02) * mm, v(147.51, 110.62) * mm, v(152.72, 110.62) * mm]});
            skFitSpline(sketch, "E523", {"points": [v(152.72, 110.62) * mm, v(156.78, 110.62) * mm, v(159.46, 109.94) * mm, v(160.79, 108.57) * mm]});
            skFitSpline(sketch, "E524", {"points": [v(160.79, 108.57) * mm, v(162.11, 107.2) * mm, v(162.93, 103.95) * mm, v(163.25, 98.82) * mm]});
            skFitSpline(sketch, "E525", {"points": [v(163.25, 98.82) * mm, v(159.1, 100.65) * mm, v(154.02, 101.57) * mm, v(148.06, 101.57) * mm]});
            skFitSpline(sketch, "E526", {"points": [v(148.06, 101.57) * mm, v(143.16, 101.57) * mm, v(138.24, 101.13) * mm, v(133.32, 100.27) * mm]});
            skFitSpline(sketch, "E527", {"points": [v(131.2, 99.92) * mm, v(129.2, 99.58) * mm, v(127.89, 99.4) * mm, v(127.26, 99.4) * mm]});
            skFitSpline(sketch, "E528", {"points": [v(127.26, 99.4) * mm, v(125.1, 99.4) * mm, v(124.04, 100.8) * mm, v(124.04, 103.6) * mm]});
            skFitSpline(sketch, "E529", {"points": [v(124.04, 103.6) * mm, v(124.04, 104.4) * mm, v(124.14, 105.62) * mm, v(124.32, 107.24) * mm]});
            skFitSpline(sketch, "E530", {"points": [v(124.32, 107.24) * mm, v(132.32, 113.12) * mm, v(139.12, 119.9) * mm, v(144.71, 127.63) * mm]});
            skFitSpline(sketch, "E531", {"points": [v(144.71, 127.63) * mm, v(150.3, 135.35) * mm, v(153.1, 141.66) * mm, v(153.1, 146.57) * mm]});
            skFitSpline(sketch, "E532", {"points": [v(153.1, 146.57) * mm, v(153.1, 151.09) * mm, v(150.85, 153.34) * mm, v(146.35, 153.34) * mm]});
            skFitSpline(sketch, "E533", {"points": [v(146.35, 153.34) * mm, v(140.98, 153.34) * mm, v(135.91, 149.75) * mm, v(131.13, 142.53) * mm]});
            skFitSpline(sketch, "E534", {"points": [v(131.13, 142.53) * mm, v(130.6, 144.51) * mm, v(130.34, 146) * mm, v(130.34, 147.01) * mm]});
            skFitSpline(sketch, "E535", {"points": [v(130.34, 147.01) * mm, v(130.34, 150.43) * mm, v(132.32, 153.57) * mm, v(136.28, 156.45) * mm]});
            skFitSpline(sketch, "E536", {"points": [v(136.28, 156.45) * mm, v(140.24, 159.33) * mm, v(144.45, 160.76) * mm, v(148.9, 160.76) * mm]});
            skFitSpline(sketch, "E537", {"points": [v(202.2, 129.7) * mm, v(201.44, 123.52) * mm, v(199.56, 120.44) * mm, v(196.58, 120.44) * mm]});
            skFitSpline(sketch, "E538", {"points": [v(196.58, 120.44) * mm, v(195.93, 120.44) * mm, v(195.18, 120.5) * mm, v(194.33, 120.6) * mm]});
            skFitSpline(sketch, "E539", {"points": [v(191.57, 120.98) * mm, v(189.87, 121.23) * mm, v(188.55, 121.35) * mm, v(187.62, 121.35) * mm]});
            skFitSpline(sketch, "E540", {"points": [v(187.62, 121.35) * mm, v(186.31, 121.35) * mm, v(184.66, 120.96) * mm, v(182.65, 120.15) * mm]});
            skFitSpline(sketch, "E541", {"points": [v(182.65, 120.15) * mm, v(184.1, 125.83) * mm, v(186.47, 128.65) * mm, v(189.74, 128.65) * mm]});
            skFitSpline(sketch, "E542", {"points": [v(189.74, 128.65) * mm, v(190.3, 128.65) * mm, v(190.9, 128.6) * mm, v(191.57, 128.53) * mm]});
            skLineSegment(sketch, "E543", {"start": v(194.33, 120.6) * mm, "end": v(191.57, 120.98) * mm});
            skLineSegment(sketch, "E544", {"start": v(191.57, 120.98) * mm, "end": v(194.33, 120.6) * mm});
            skFitSpline(sketch, "E545", {"points": [v(195.42, 128.04) * mm, v(196.04, 127.97) * mm, v(196.72, 127.94) * mm, v(197.45, 127.94) * mm]});
            skFitSpline(sketch, "E546", {"points": [v(197.45, 127.94) * mm, v(199.07, 127.94) * mm, v(200.66, 128.53) * mm, v(202.2, 129.7) * mm]});
            skLineSegment(sketch, "E547", {"start": v(191.57, 128.53) * mm, "end": v(195.42, 128.04) * mm});
            skLineSegment(sketch, "E548", {"start": v(195.42, 128.04) * mm, "end": v(191.57, 128.53) * mm});
            skFitSpline(sketch, "E549", {"points": [v(202.2, 129.7) * mm, v(201.44, 123.52) * mm, v(199.56, 120.44) * mm, v(196.58, 120.44) * mm]});
            skFitSpline(sketch, "E550", {"points": [v(196.58, 120.44) * mm, v(195.93, 120.44) * mm, v(195.18, 120.5) * mm, v(194.33, 120.6) * mm]});
            skFitSpline(sketch, "E551", {"points": [v(191.57, 120.98) * mm, v(189.87, 121.23) * mm, v(188.55, 121.35) * mm, v(187.62, 121.35) * mm]});
            skFitSpline(sketch, "E552", {"points": [v(187.62, 121.35) * mm, v(186.31, 121.35) * mm, v(184.66, 120.96) * mm, v(182.65, 120.15) * mm]});
            skFitSpline(sketch, "E553", {"points": [v(182.65, 120.15) * mm, v(184.1, 125.83) * mm, v(186.47, 128.65) * mm, v(189.74, 128.65) * mm]});
            skFitSpline(sketch, "E554", {"points": [v(189.74, 128.65) * mm, v(190.3, 128.65) * mm, v(190.9, 128.6) * mm, v(191.57, 128.53) * mm]});
            skFitSpline(sketch, "E555", {"points": [v(195.42, 128.04) * mm, v(196.04, 127.97) * mm, v(196.72, 127.94) * mm, v(197.45, 127.94) * mm]});
            skFitSpline(sketch, "E556", {"points": [v(197.45, 127.94) * mm, v(199.07, 127.94) * mm, v(200.66, 128.53) * mm, v(202.2, 129.7) * mm]});
            skFitSpline(sketch, "E557", {"points": [v(231.1, 107.4) * mm, v(233.12, 107.8) * mm, v(234.8, 107.99) * mm, v(236.16, 107.99) * mm]});
            skFitSpline(sketch, "E558", {"points": [v(236.16, 107.99) * mm, v(239.42, 107.99) * mm, v(241.64, 107.39) * mm, v(242.8, 106.17) * mm]});
            skFitSpline(sketch, "E559", {"points": [v(242.8, 106.17) * mm, v(243.98, 104.96) * mm, v(244.56, 102.4) * mm, v(244.56, 98.48) * mm]});
            skFitSpline(sketch, "E560", {"points": [v(244.56, 98.48) * mm, v(242.68, 99.4) * mm, v(240.77, 99.85) * mm, v(238.84, 99.85) * mm]});
            skFitSpline(sketch, "E561", {"points": [v(238.84, 99.85) * mm, v(236.6, 99.85) * mm, v(233.83, 99.62) * mm, v(230.56, 99.18) * mm]});
            skLineSegment(sketch, "E562", {"start": v(240.33, 160.84) * mm, "end": v(231.1, 107.4) * mm});
            skLineSegment(sketch, "E563", {"start": v(231.1, 107.4) * mm, "end": v(240.33, 160.84) * mm});
            skFitSpline(sketch, "E564", {"points": [v(225.68, 98.5) * mm, v(224.08, 98.26) * mm, v(221.9, 97.9) * mm, v(219.13, 97.41) * mm]});
            skFitSpline(sketch, "E565", {"points": [v(219.13, 97.41) * mm, v(218.25, 97.25) * mm, v(217.34, 97.17) * mm, v(216.4, 97.17) * mm]});
            skFitSpline(sketch, "E566", {"points": [v(216.4, 97.17) * mm, v(213.42, 97.17) * mm, v(211.7, 100.17) * mm, v(211.24, 106.14) * mm]});
            skFitSpline(sketch, "E567", {"points": [v(211.24, 106.14) * mm, v(213.04, 105.46) * mm, v(214.48, 105.12) * mm, v(215.58, 105.12) * mm]});
            skFitSpline(sketch, "E568", {"points": [v(215.58, 105.12) * mm, v(218.04, 105.12) * mm, v(220.36, 105.41) * mm, v(222.57, 106) * mm]});
            skLineSegment(sketch, "E569", {"start": v(230.56, 99.18) * mm, "end": v(225.68, 98.5) * mm});
            skLineSegment(sketch, "E570", {"start": v(225.68, 98.5) * mm, "end": v(230.56, 99.18) * mm});
            skFitSpline(sketch, "E571", {"points": [v(230.14, 148.1) * mm, v(226.91, 146) * mm, v(224.12, 144.93) * mm, v(221.77, 144.93) * mm]});
            skFitSpline(sketch, "E572", {"points": [v(221.77, 144.93) * mm, v(217.95, 144.93) * mm, v(216.04, 147.62) * mm, v(216.04, 153.01) * mm]});
            skLineSegment(sketch, "E573", {"start": v(222.57, 106) * mm, "end": v(230.14, 148.1) * mm});
            skLineSegment(sketch, "E574", {"start": v(230.14, 148.1) * mm, "end": v(222.57, 106) * mm});
            skFitSpline(sketch, "E575", {"points": [v(216.04, 154.9) * mm, v(218.1, 153.52) * mm, v(219.94, 152.83) * mm, v(221.59, 152.83) * mm]});
            skFitSpline(sketch, "E576", {"points": [v(221.59, 152.83) * mm, v(224.5, 152.83) * mm, v(229.56, 155.03) * mm, v(236.73, 159.44) * mm]});
            skFitSpline(sketch, "E577", {"points": [v(236.73, 159.44) * mm, v(237.05, 159.62) * mm, v(238.25, 160.1) * mm, v(240.33, 160.84) * mm]});
            skLineSegment(sketch, "E578", {"start": v(216.04, 153.01) * mm, "end": v(216.04, 154.9) * mm});
            skLineSegment(sketch, "E579", {"start": v(216.04, 154.9) * mm, "end": v(216.04, 153.01) * mm});
            skFitSpline(sketch, "E580", {"points": [v(231.1, 107.4) * mm, v(233.12, 107.8) * mm, v(234.8, 107.99) * mm, v(236.16, 107.99) * mm]});
            skFitSpline(sketch, "E581", {"points": [v(236.16, 107.99) * mm, v(239.42, 107.99) * mm, v(241.64, 107.39) * mm, v(242.8, 106.17) * mm]});
            skFitSpline(sketch, "E582", {"points": [v(242.8, 106.17) * mm, v(243.98, 104.96) * mm, v(244.56, 102.4) * mm, v(244.56, 98.48) * mm]});
            skFitSpline(sketch, "E583", {"points": [v(244.56, 98.48) * mm, v(242.68, 99.4) * mm, v(240.77, 99.85) * mm, v(238.84, 99.85) * mm]});
            skFitSpline(sketch, "E584", {"points": [v(238.84, 99.85) * mm, v(236.6, 99.85) * mm, v(233.83, 99.62) * mm, v(230.56, 99.18) * mm]});
            skFitSpline(sketch, "E585", {"points": [v(225.68, 98.5) * mm, v(224.08, 98.26) * mm, v(221.9, 97.9) * mm, v(219.13, 97.41) * mm]});
            skFitSpline(sketch, "E586", {"points": [v(219.13, 97.41) * mm, v(218.25, 97.25) * mm, v(217.34, 97.17) * mm, v(216.4, 97.17) * mm]});
            skFitSpline(sketch, "E587", {"points": [v(216.4, 97.17) * mm, v(213.42, 97.17) * mm, v(211.7, 100.17) * mm, v(211.24, 106.14) * mm]});
            skFitSpline(sketch, "E588", {"points": [v(211.24, 106.14) * mm, v(213.04, 105.46) * mm, v(214.48, 105.12) * mm, v(215.58, 105.12) * mm]});
            skFitSpline(sketch, "E589", {"points": [v(215.58, 105.12) * mm, v(218.04, 105.12) * mm, v(220.36, 105.41) * mm, v(222.57, 106) * mm]});
            skFitSpline(sketch, "E590", {"points": [v(230.14, 148.1) * mm, v(226.91, 146) * mm, v(224.12, 144.93) * mm, v(221.77, 144.93) * mm]});
            skFitSpline(sketch, "E591", {"points": [v(221.77, 144.93) * mm, v(217.95, 144.93) * mm, v(216.04, 147.62) * mm, v(216.04, 153.01) * mm]});
            skFitSpline(sketch, "E592", {"points": [v(216.04, 154.9) * mm, v(218.1, 153.52) * mm, v(219.94, 152.83) * mm, v(221.59, 152.83) * mm]});
            skFitSpline(sketch, "E593", {"points": [v(221.59, 152.83) * mm, v(224.5, 152.83) * mm, v(229.56, 155.03) * mm, v(236.73, 159.44) * mm]});
            skFitSpline(sketch, "E594", {"points": [v(236.73, 159.44) * mm, v(237.05, 159.62) * mm, v(238.25, 160.1) * mm, v(240.33, 160.84) * mm]});
            skFitSpline(sketch, "E595", {"points": [v(280.08, 107.4) * mm, v(282.1, 107.8) * mm, v(283.8, 107.99) * mm, v(285.15, 107.99) * mm]});
            skFitSpline(sketch, "E596", {"points": [v(285.15, 107.99) * mm, v(288.4, 107.99) * mm, v(290.62, 107.39) * mm, v(291.8, 106.17) * mm]});
            skFitSpline(sketch, "E597", {"points": [v(291.8, 106.17) * mm, v(292.97, 104.96) * mm, v(293.54, 102.4) * mm, v(293.54, 98.48) * mm]});
            skFitSpline(sketch, "E598", {"points": [v(293.54, 98.48) * mm, v(291.66, 99.4) * mm, v(289.75, 99.85) * mm, v(287.82, 99.85) * mm]});
            skFitSpline(sketch, "E599", {"points": [v(287.82, 99.85) * mm, v(285.58, 99.85) * mm, v(282.82, 99.62) * mm, v(279.55, 99.18) * mm]});
            skLineSegment(sketch, "E600", {"start": v(289.32, 160.84) * mm, "end": v(280.08, 107.4) * mm});
            skLineSegment(sketch, "E601", {"start": v(280.08, 107.4) * mm, "end": v(289.32, 160.84) * mm});
            skFitSpline(sketch, "E602", {"points": [v(274.67, 98.5) * mm, v(273.07, 98.26) * mm, v(270.89, 97.9) * mm, v(268.12, 97.41) * mm]});
            skFitSpline(sketch, "E603", {"points": [v(268.12, 97.41) * mm, v(267.24, 97.25) * mm, v(266.33, 97.17) * mm, v(265.4, 97.17) * mm]});
            skFitSpline(sketch, "E604", {"points": [v(265.4, 97.17) * mm, v(262.41, 97.17) * mm, v(260.68, 100.17) * mm, v(260.23, 106.14) * mm]});
            skFitSpline(sketch, "E605", {"points": [v(260.23, 106.14) * mm, v(262.03, 105.46) * mm, v(263.47, 105.12) * mm, v(264.56, 105.12) * mm]});
            skFitSpline(sketch, "E606", {"points": [v(264.56, 105.12) * mm, v(267.03, 105.12) * mm, v(269.35, 105.41) * mm, v(271.55, 106) * mm]});
            skLineSegment(sketch, "E607", {"start": v(279.55, 99.18) * mm, "end": v(274.67, 98.5) * mm});
            skLineSegment(sketch, "E608", {"start": v(274.67, 98.5) * mm, "end": v(279.55, 99.18) * mm});
            skFitSpline(sketch, "E609", {"points": [v(279.12, 148.1) * mm, v(275.9, 146) * mm, v(273.11, 144.93) * mm, v(270.76, 144.93) * mm]});
            skFitSpline(sketch, "E610", {"points": [v(270.76, 144.93) * mm, v(266.94, 144.93) * mm, v(265.03, 147.62) * mm, v(265.03, 153.01) * mm]});
            skLineSegment(sketch, "E611", {"start": v(271.55, 106) * mm, "end": v(279.12, 148.1) * mm});
            skLineSegment(sketch, "E612", {"start": v(279.12, 148.1) * mm, "end": v(271.55, 106) * mm});
            skFitSpline(sketch, "E613", {"points": [v(265.03, 154.9) * mm, v(267.08, 153.52) * mm, v(268.93, 152.83) * mm, v(270.57, 152.83) * mm]});
            skFitSpline(sketch, "E614", {"points": [v(270.57, 152.83) * mm, v(273.5, 152.83) * mm, v(278.55, 155.03) * mm, v(285.72, 159.44) * mm]});
            skFitSpline(sketch, "E615", {"points": [v(285.72, 159.44) * mm, v(286.03, 159.62) * mm, v(287.24, 160.1) * mm, v(289.32, 160.84) * mm]});
            skLineSegment(sketch, "E616", {"start": v(265.03, 153.01) * mm, "end": v(265.03, 154.9) * mm});
            skLineSegment(sketch, "E617", {"start": v(265.03, 154.9) * mm, "end": v(265.03, 153.01) * mm});
            skFitSpline(sketch, "E618", {"points": [v(280.08, 107.4) * mm, v(282.1, 107.8) * mm, v(283.8, 107.99) * mm, v(285.15, 107.99) * mm]});
            skFitSpline(sketch, "E619", {"points": [v(285.15, 107.99) * mm, v(288.4, 107.99) * mm, v(290.62, 107.39) * mm, v(291.8, 106.17) * mm]});
            skFitSpline(sketch, "E620", {"points": [v(291.8, 106.17) * mm, v(292.97, 104.96) * mm, v(293.54, 102.4) * mm, v(293.54, 98.48) * mm]});
            skFitSpline(sketch, "E621", {"points": [v(293.54, 98.48) * mm, v(291.66, 99.4) * mm, v(289.75, 99.85) * mm, v(287.82, 99.85) * mm]});
            skFitSpline(sketch, "E622", {"points": [v(287.82, 99.85) * mm, v(285.58, 99.85) * mm, v(282.82, 99.62) * mm, v(279.55, 99.18) * mm]});
            skFitSpline(sketch, "E623", {"points": [v(274.67, 98.5) * mm, v(273.07, 98.26) * mm, v(270.89, 97.9) * mm, v(268.12, 97.41) * mm]});
            skFitSpline(sketch, "E624", {"points": [v(268.12, 97.41) * mm, v(267.24, 97.25) * mm, v(266.33, 97.17) * mm, v(265.4, 97.17) * mm]});
            skFitSpline(sketch, "E625", {"points": [v(265.4, 97.17) * mm, v(262.41, 97.17) * mm, v(260.68, 100.17) * mm, v(260.23, 106.14) * mm]});
            skFitSpline(sketch, "E626", {"points": [v(260.23, 106.14) * mm, v(262.03, 105.46) * mm, v(263.47, 105.12) * mm, v(264.56, 105.12) * mm]});
            skFitSpline(sketch, "E627", {"points": [v(264.56, 105.12) * mm, v(267.03, 105.12) * mm, v(269.35, 105.41) * mm, v(271.55, 106) * mm]});
            skFitSpline(sketch, "E628", {"points": [v(279.12, 148.1) * mm, v(275.9, 146) * mm, v(273.11, 144.93) * mm, v(270.76, 144.93) * mm]});
            skFitSpline(sketch, "E629", {"points": [v(270.76, 144.93) * mm, v(266.94, 144.93) * mm, v(265.03, 147.62) * mm, v(265.03, 153.01) * mm]});
            skFitSpline(sketch, "E630", {"points": [v(265.03, 154.9) * mm, v(267.08, 153.52) * mm, v(268.93, 152.83) * mm, v(270.57, 152.83) * mm]});
            skFitSpline(sketch, "E631", {"points": [v(270.57, 152.83) * mm, v(273.5, 152.83) * mm, v(278.55, 155.03) * mm, v(285.72, 159.44) * mm]});
            skFitSpline(sketch, "E632", {"points": [v(285.72, 159.44) * mm, v(286.03, 159.62) * mm, v(287.24, 160.1) * mm, v(289.32, 160.84) * mm]});
            skFitSpline(sketch, "E633", {"points": [v(335.1, 129.7) * mm, v(334.33, 123.52) * mm, v(332.46, 120.44) * mm, v(329.47, 120.44) * mm]});
            skFitSpline(sketch, "E634", {"points": [v(329.47, 120.44) * mm, v(328.83, 120.44) * mm, v(328.08, 120.5) * mm, v(327.22, 120.6) * mm]});
            skFitSpline(sketch, "E635", {"points": [v(324.46, 120.98) * mm, v(322.76, 121.23) * mm, v(321.44, 121.35) * mm, v(320.51, 121.35) * mm]});
            skFitSpline(sketch, "E636", {"points": [v(320.51, 121.35) * mm, v(319.2, 121.35) * mm, v(317.55, 120.96) * mm, v(315.55, 120.15) * mm]});
            skFitSpline(sketch, "E637", {"points": [v(315.55, 120.15) * mm, v(317, 125.83) * mm, v(319.37, 128.65) * mm, v(322.63, 128.65) * mm]});
            skFitSpline(sketch, "E638", {"points": [v(322.63, 128.65) * mm, v(323.19, 128.65) * mm, v(323.8, 128.6) * mm, v(324.46, 128.53) * mm]});
            skLineSegment(sketch, "E639", {"start": v(327.22, 120.6) * mm, "end": v(324.46, 120.98) * mm});
            skLineSegment(sketch, "E640", {"start": v(324.46, 120.98) * mm, "end": v(327.22, 120.6) * mm});
            skFitSpline(sketch, "E641", {"points": [v(328.31, 128.04) * mm, v(328.94, 127.97) * mm, v(329.62, 127.94) * mm, v(330.34, 127.94) * mm]});
            skFitSpline(sketch, "E642", {"points": [v(330.34, 127.94) * mm, v(331.97, 127.94) * mm, v(333.56, 128.53) * mm, v(335.1, 129.7) * mm]});
            skLineSegment(sketch, "E643", {"start": v(324.46, 128.53) * mm, "end": v(328.31, 128.04) * mm});
            skLineSegment(sketch, "E644", {"start": v(328.31, 128.04) * mm, "end": v(324.46, 128.53) * mm});
            skFitSpline(sketch, "E645", {"points": [v(335.1, 129.7) * mm, v(334.33, 123.52) * mm, v(332.46, 120.44) * mm, v(329.47, 120.44) * mm]});
            skFitSpline(sketch, "E646", {"points": [v(329.47, 120.44) * mm, v(328.83, 120.44) * mm, v(328.08, 120.5) * mm, v(327.22, 120.6) * mm]});
            skFitSpline(sketch, "E647", {"points": [v(324.46, 120.98) * mm, v(322.76, 121.23) * mm, v(321.44, 121.35) * mm, v(320.51, 121.35) * mm]});
            skFitSpline(sketch, "E648", {"points": [v(320.51, 121.35) * mm, v(319.2, 121.35) * mm, v(317.55, 120.96) * mm, v(315.55, 120.15) * mm]});
            skFitSpline(sketch, "E649", {"points": [v(315.55, 120.15) * mm, v(317, 125.83) * mm, v(319.37, 128.65) * mm, v(322.63, 128.65) * mm]});
            skFitSpline(sketch, "E650", {"points": [v(322.63, 128.65) * mm, v(323.19, 128.65) * mm, v(323.8, 128.6) * mm, v(324.46, 128.53) * mm]});
            skFitSpline(sketch, "E651", {"points": [v(328.31, 128.04) * mm, v(328.94, 127.97) * mm, v(329.62, 127.94) * mm, v(330.34, 127.94) * mm]});
            skFitSpline(sketch, "E652", {"points": [v(330.34, 127.94) * mm, v(331.97, 127.94) * mm, v(333.56, 128.53) * mm, v(335.1, 129.7) * mm]});
            skFitSpline(sketch, "E653", {"points": [v(364.48, 107.4) * mm, v(366.5, 107.8) * mm, v(368.19, 107.99) * mm, v(369.54, 107.99) * mm]});
            skFitSpline(sketch, "E654", {"points": [v(369.54, 107.99) * mm, v(372.8, 107.99) * mm, v(375.02, 107.39) * mm, v(376.19, 106.17) * mm]});
            skFitSpline(sketch, "E655", {"points": [v(376.19, 106.17) * mm, v(377.36, 104.96) * mm, v(377.94, 102.4) * mm, v(377.94, 98.48) * mm]});
            skFitSpline(sketch, "E656", {"points": [v(377.94, 98.48) * mm, v(376.06, 99.4) * mm, v(374.15, 99.85) * mm, v(372.22, 99.85) * mm]});
            skFitSpline(sketch, "E657", {"points": [v(372.22, 99.85) * mm, v(369.97, 99.85) * mm, v(367.22, 99.62) * mm, v(363.94, 99.18) * mm]});
            skLineSegment(sketch, "E658", {"start": v(373.71, 160.84) * mm, "end": v(364.48, 107.4) * mm});
            skLineSegment(sketch, "E659", {"start": v(364.48, 107.4) * mm, "end": v(373.71, 160.84) * mm});
            skFitSpline(sketch, "E660", {"points": [v(359.06, 98.5) * mm, v(357.46, 98.26) * mm, v(355.28, 97.9) * mm, v(352.51, 97.41) * mm]});
            skFitSpline(sketch, "E661", {"points": [v(352.51, 97.41) * mm, v(351.63, 97.25) * mm, v(350.72, 97.17) * mm, v(349.78, 97.17) * mm]});
            skFitSpline(sketch, "E662", {"points": [v(349.78, 97.17) * mm, v(346.8, 97.17) * mm, v(345.08, 100.17) * mm, v(344.62, 106.14) * mm]});
            skFitSpline(sketch, "E663", {"points": [v(344.62, 106.14) * mm, v(346.42, 105.46) * mm, v(347.86, 105.12) * mm, v(348.96, 105.12) * mm]});
            skFitSpline(sketch, "E664", {"points": [v(348.96, 105.12) * mm, v(351.42, 105.12) * mm, v(353.75, 105.41) * mm, v(355.95, 106) * mm]});
            skLineSegment(sketch, "E665", {"start": v(363.94, 99.18) * mm, "end": v(359.06, 98.5) * mm});
            skLineSegment(sketch, "E666", {"start": v(359.06, 98.5) * mm, "end": v(363.94, 99.18) * mm});
            skFitSpline(sketch, "E667", {"points": [v(363.52, 148.1) * mm, v(360.3, 146) * mm, v(357.5, 144.93) * mm, v(355.15, 144.93) * mm]});
            skFitSpline(sketch, "E668", {"points": [v(355.15, 144.93) * mm, v(351.33, 144.93) * mm, v(349.42, 147.62) * mm, v(349.42, 153.01) * mm]});
            skLineSegment(sketch, "E669", {"start": v(355.95, 106) * mm, "end": v(363.52, 148.1) * mm});
            skLineSegment(sketch, "E670", {"start": v(363.52, 148.1) * mm, "end": v(355.95, 106) * mm});
            skFitSpline(sketch, "E671", {"points": [v(349.42, 154.9) * mm, v(351.47, 153.52) * mm, v(353.32, 152.83) * mm, v(354.97, 152.83) * mm]});
            skFitSpline(sketch, "E672", {"points": [v(354.97, 152.83) * mm, v(357.89, 152.83) * mm, v(362.94, 155.03) * mm, v(370.12, 159.44) * mm]});
            skFitSpline(sketch, "E673", {"points": [v(370.12, 159.44) * mm, v(370.43, 159.62) * mm, v(371.63, 160.1) * mm, v(373.71, 160.84) * mm]});
            skLineSegment(sketch, "E674", {"start": v(349.42, 153.01) * mm, "end": v(349.42, 154.9) * mm});
            skLineSegment(sketch, "E675", {"start": v(349.42, 154.9) * mm, "end": v(349.42, 153.01) * mm});
            skFitSpline(sketch, "E676", {"points": [v(399.53, 161.29) * mm, v(401.74, 160.06) * mm, v(404.75, 159.45) * mm, v(408.55, 159.45) * mm]});
            skFitSpline(sketch, "E677", {"points": [v(432.57, 150.65) * mm, v(425.06, 143.33) * mm, v(418.97, 135.14) * mm, v(414.28, 126.1) * mm]});
            skFitSpline(sketch, "E678", {"points": [v(414.28, 126.1) * mm, v(409.6, 117.05) * mm, v(407.25, 109.05) * mm, v(407.25, 102.1) * mm]});
            skFitSpline(sketch, "E679", {"points": [v(407.25, 102.1) * mm, v(407.25, 100.52) * mm, v(407.42, 98.58) * mm, v(407.77, 96.28) * mm]});
            skFitSpline(sketch, "E680", {"points": [v(407.77, 96.28) * mm, v(406.64, 95.93) * mm, v(405.75, 95.74) * mm, v(405.08, 95.74) * mm]});
            skFitSpline(sketch, "E681", {"points": [v(405.08, 95.74) * mm, v(400.09, 95.74) * mm, v(397.59, 97.79) * mm, v(397.59, 101.86) * mm]});
            skFitSpline(sketch, "E682", {"points": [v(397.59, 101.86) * mm, v(397.59, 104.73) * mm, v(398.72, 109.17) * mm, v(401, 115.15) * mm]});
            skFitSpline(sketch, "E683", {"points": [v(401, 115.15) * mm, v(403.29, 121.13) * mm, v(405.8, 126.31) * mm, v(408.57, 130.72) * mm]});
            skFitSpline(sketch, "E684", {"points": [v(408.57, 130.72) * mm, v(414.11, 139.56) * mm, v(419.76, 146.08) * mm, v(425.54, 150.28) * mm]});
            skLineSegment(sketch, "E685", {"start": v(408.55, 159.45) * mm, "end": v(410.1, 159.48) * mm});
            skLineSegment(sketch, "E686", {"start": v(410.1, 159.48) * mm, "end": v(414.9, 159.4) * mm});
            skLineSegment(sketch, "E687", {"start": v(414.9, 159.4) * mm, "end": v(419.69, 159.33) * mm});
            skLineSegment(sketch, "E688", {"start": v(419.69, 159.33) * mm, "end": v(433.97, 159.33) * mm});
            skLineSegment(sketch, "E689", {"start": v(433.97, 159.33) * mm, "end": v(432.57, 150.65) * mm});
            skFitSpline(sketch, "E690", {"points": [v(411.55, 150.23) * mm, v(406.34, 150.23) * mm, v(402.84, 150.48) * mm, v(401.06, 150.98) * mm]});
            skFitSpline(sketch, "E691", {"points": [v(401.06, 150.98) * mm, v(399.28, 151.48) * mm, v(398.39, 152.65) * mm, v(398.39, 154.51) * mm]});
            skFitSpline(sketch, "E692", {"points": [v(398.39, 154.51) * mm, v(398.39, 155.11) * mm, v(398.47, 155.9) * mm, v(398.64, 156.83) * mm]});
            skFitSpline(sketch, "E693", {"points": [v(398.64, 156.83) * mm, v(398.73, 157.24) * mm, v(398.84, 157.8) * mm, v(398.98, 158.52) * mm]});
            skLineSegment(sketch, "E694", {"start": v(425.54, 150.28) * mm, "end": v(413.55, 150.28) * mm});
            skLineSegment(sketch, "E695", {"start": v(413.55, 150.28) * mm, "end": v(411.55, 150.23) * mm});
            skLineSegment(sketch, "E696", {"start": v(411.55, 150.23) * mm, "end": v(425.54, 150.28) * mm});
            skLineSegment(sketch, "E697", {"start": v(398.98, 158.52) * mm, "end": v(399.53, 161.29) * mm});
            skLineSegment(sketch, "E698", {"start": v(399.53, 161.29) * mm, "end": v(398.98, 158.52) * mm});
            skFitSpline(sketch, "E699", {"points": [v(364.48, 107.4) * mm, v(366.5, 107.8) * mm, v(368.19, 107.99) * mm, v(369.54, 107.99) * mm]});
            skFitSpline(sketch, "E700", {"points": [v(369.54, 107.99) * mm, v(372.8, 107.99) * mm, v(375.02, 107.39) * mm, v(376.19, 106.17) * mm]});
            skFitSpline(sketch, "E701", {"points": [v(376.19, 106.17) * mm, v(377.36, 104.96) * mm, v(377.94, 102.4) * mm, v(377.94, 98.48) * mm]});
            skFitSpline(sketch, "E702", {"points": [v(377.94, 98.48) * mm, v(376.06, 99.4) * mm, v(374.15, 99.85) * mm, v(372.22, 99.85) * mm]});
            skFitSpline(sketch, "E703", {"points": [v(372.22, 99.85) * mm, v(369.97, 99.85) * mm, v(367.22, 99.62) * mm, v(363.94, 99.18) * mm]});
            skFitSpline(sketch, "E704", {"points": [v(359.06, 98.5) * mm, v(357.46, 98.26) * mm, v(355.28, 97.9) * mm, v(352.51, 97.41) * mm]});
            skFitSpline(sketch, "E705", {"points": [v(352.51, 97.41) * mm, v(351.63, 97.25) * mm, v(350.72, 97.17) * mm, v(349.78, 97.17) * mm]});
            skFitSpline(sketch, "E706", {"points": [v(349.78, 97.17) * mm, v(346.8, 97.17) * mm, v(345.08, 100.17) * mm, v(344.62, 106.14) * mm]});
            skFitSpline(sketch, "E707", {"points": [v(344.62, 106.14) * mm, v(346.42, 105.46) * mm, v(347.86, 105.12) * mm, v(348.96, 105.12) * mm]});
            skFitSpline(sketch, "E708", {"points": [v(348.96, 105.12) * mm, v(351.42, 105.12) * mm, v(353.75, 105.41) * mm, v(355.95, 106) * mm]});
            skFitSpline(sketch, "E709", {"points": [v(363.52, 148.1) * mm, v(360.3, 146) * mm, v(357.5, 144.93) * mm, v(355.15, 144.93) * mm]});
            skFitSpline(sketch, "E710", {"points": [v(355.15, 144.93) * mm, v(351.33, 144.93) * mm, v(349.42, 147.62) * mm, v(349.42, 153.01) * mm]});
            skFitSpline(sketch, "E711", {"points": [v(349.42, 154.9) * mm, v(351.47, 153.52) * mm, v(353.32, 152.83) * mm, v(354.97, 152.83) * mm]});
            skFitSpline(sketch, "E712", {"points": [v(354.97, 152.83) * mm, v(357.89, 152.83) * mm, v(362.94, 155.03) * mm, v(370.12, 159.44) * mm]});
            skFitSpline(sketch, "E713", {"points": [v(370.12, 159.44) * mm, v(370.43, 159.62) * mm, v(371.63, 160.1) * mm, v(373.71, 160.84) * mm]});
            skFitSpline(sketch, "E714", {"points": [v(399.53, 161.29) * mm, v(401.74, 160.06) * mm, v(404.75, 159.45) * mm, v(408.55, 159.45) * mm]});
            skFitSpline(sketch, "E715", {"points": [v(432.57, 150.65) * mm, v(425.06, 143.33) * mm, v(418.97, 135.14) * mm, v(414.28, 126.1) * mm]});
            skFitSpline(sketch, "E716", {"points": [v(414.28, 126.1) * mm, v(409.6, 117.05) * mm, v(407.25, 109.05) * mm, v(407.25, 102.1) * mm]});
            skFitSpline(sketch, "E717", {"points": [v(407.25, 102.1) * mm, v(407.25, 100.52) * mm, v(407.42, 98.58) * mm, v(407.77, 96.28) * mm]});
            skFitSpline(sketch, "E718", {"points": [v(407.77, 96.28) * mm, v(406.64, 95.93) * mm, v(405.75, 95.74) * mm, v(405.08, 95.74) * mm]});
            skFitSpline(sketch, "E719", {"points": [v(405.08, 95.74) * mm, v(400.09, 95.74) * mm, v(397.59, 97.79) * mm, v(397.59, 101.86) * mm]});
            skFitSpline(sketch, "E720", {"points": [v(397.59, 101.86) * mm, v(397.59, 104.73) * mm, v(398.72, 109.17) * mm, v(401, 115.15) * mm]});
            skFitSpline(sketch, "E721", {"points": [v(401, 115.15) * mm, v(403.29, 121.13) * mm, v(405.8, 126.31) * mm, v(408.57, 130.72) * mm]});
            skFitSpline(sketch, "E722", {"points": [v(408.57, 130.72) * mm, v(414.11, 139.56) * mm, v(419.76, 146.08) * mm, v(425.54, 150.28) * mm]});
            skFitSpline(sketch, "E723", {"points": [v(411.55, 150.23) * mm, v(406.34, 150.23) * mm, v(402.84, 150.48) * mm, v(401.06, 150.98) * mm]});
            skFitSpline(sketch, "E724", {"points": [v(401.06, 150.98) * mm, v(399.28, 151.48) * mm, v(398.39, 152.65) * mm, v(398.39, 154.51) * mm]});
            skFitSpline(sketch, "E725", {"points": [v(398.39, 154.51) * mm, v(398.39, 155.11) * mm, v(398.47, 155.9) * mm, v(398.64, 156.83) * mm]});
            skFitSpline(sketch, "E726", {"points": [v(398.64, 156.83) * mm, v(398.73, 157.24) * mm, v(398.84, 157.8) * mm, v(398.98, 158.52) * mm]});
            skLineSegment(sketch, "E727", {"start": v(279.4, 609.6) * mm, "end": v(278.58, 0) * mm, "construction": true});
            skArc(sketch, "E728.filletArc", {"start": v(265.13, 241.29) * mm, "mid": v(264.88, 241.75) * mm, "end": v(264.38, 241.6) * mm});
            skArc(sketch, "E729.filletArc", {"start": v(272.83, 239.95) * mm, "mid": v(273.12, 239.47) * mm, "end": v(273.63, 239.7) * mm});
            skArc(sketch, "E730.filletArc", {"start": v(370.1, 230.58) * mm, "mid": v(370.44, 230.24) * mm, "end": v(370.88, 230.46) * mm});
            skSolve(sketch);
        }
        {
            var Q0;
            Q0=qSketchRegion(id+"F2",true);
            extrude(context, id + "F3", {"entities" : qUnion([Q0]), "operationType" : NewBodyOperationType.REMOVE, "oppositeDirection" : true, "depth" : 4.76 * mm});
        }
        {
            var Q0;
            {var subQ0=sQuery(id+"F0.wireOp",EDGE,"E4.filletArc");var subQ1=sQuery(id+"F0.wireOp",EDGE,"E3.filletArc");var subQ2=sQuery(id+"F0.wireOp",EDGE,"E2.filletArc");var subQ3=sQuery(id+"F0.wireOp",EDGE,"E1.filletArc");var subQ4=sQuery(id+"F0.wireOp",EDGE,"E0.bottom");var subQ5=sQuery(id+"F0.wireOp",EDGE,"E0.right");var subQ6=sQuery(id+"F0.wireOp",EDGE,"E0.top");var subQ7=sQuery(id+"F0.wireOp",EDGE,"E0.left");Q0=makeQuery(id+"F3.boolean.opBoolean","SPLIT",FACE,{"disambiguationData":[TD([makeQuery(id+"F1.opExtrude","SWEPT_FACE",FACE,{"disambiguationData":[OSD([subQ4])]})])],"derivedFrom":makeQuery(id+"F1.opExtrude","CAP_FACE",FACE,{"disambiguationData":[OSD([subQ4,subQ6,subQ7,subQ5,subQ3,subQ2,subQ1,subQ0])],"isStart":false})});}
            var sketch = newSketch(context, id + "F4", { "sketchPlane" : qUnion([Q0])});
            skLineSegment(sketch, "E731.bottom", {"start": v(0, 299.15) * mm, "end": v(558.8, 299.15) * mm});
            skLineSegment(sketch, "E731.top", {"start": v(0, 188.02) * mm, "end": v(558.8, 188.02) * mm});
            skLineSegment(sketch, "E732.0", {"start": v(0, 12.7) * mm, "end": v(0, 188.02) * mm});
            skArc(sketch, "E733.0", {"start": v(0, 12.7) * mm, "mid": v(3.72, 3.72) * mm, "end": v(12.7, 0) * mm});
            skLineSegment(sketch, "E734.0", {"start": v(12.7, 0) * mm, "end": v(546.1, 0) * mm});
            skArc(sketch, "E735.0", {"start": v(546.1, 0) * mm, "mid": v(555.08, 3.72) * mm, "end": v(558.8, 12.7) * mm});
            skLineSegment(sketch, "E735.1", {"start": v(558.8, 12.7) * mm, "end": v(558.8, 188.02) * mm});
            skLineSegment(sketch, "E736.trimOffspring", {"start": v(0, 299.15) * mm, "end": v(0, 596.9) * mm});
            skLineSegment(sketch, "E737.trimOffspring", {"start": v(558.8, 299.15) * mm, "end": v(558.8, 596.9) * mm});
            skArc(sketch, "E738.0", {"start": v(12.7, 609.6) * mm, "mid": v(3.72, 605.88) * mm, "end": v(0, 596.9) * mm});
            skLineSegment(sketch, "E738.1", {"start": v(12.7, 609.6) * mm, "end": v(546.1, 609.6) * mm});
            skArc(sketch, "E739.0", {"start": v(558.8, 596.9) * mm, "mid": v(555.08, 605.88) * mm, "end": v(546.1, 609.6) * mm});
            skSolve(sketch);
        }
        {
            var Q0;
            Q0=qSketchRegion(id+"F4",true);
            extrude(context, id + "F5", {"entities" : qUnion([Q0]), "operationType" : NewBodyOperationType.REMOVE, "endBound" : BoundingType.THROUGH_ALL, "oppositeDirection" : true, "depth" : 25.4 * mm});
        }
    });
